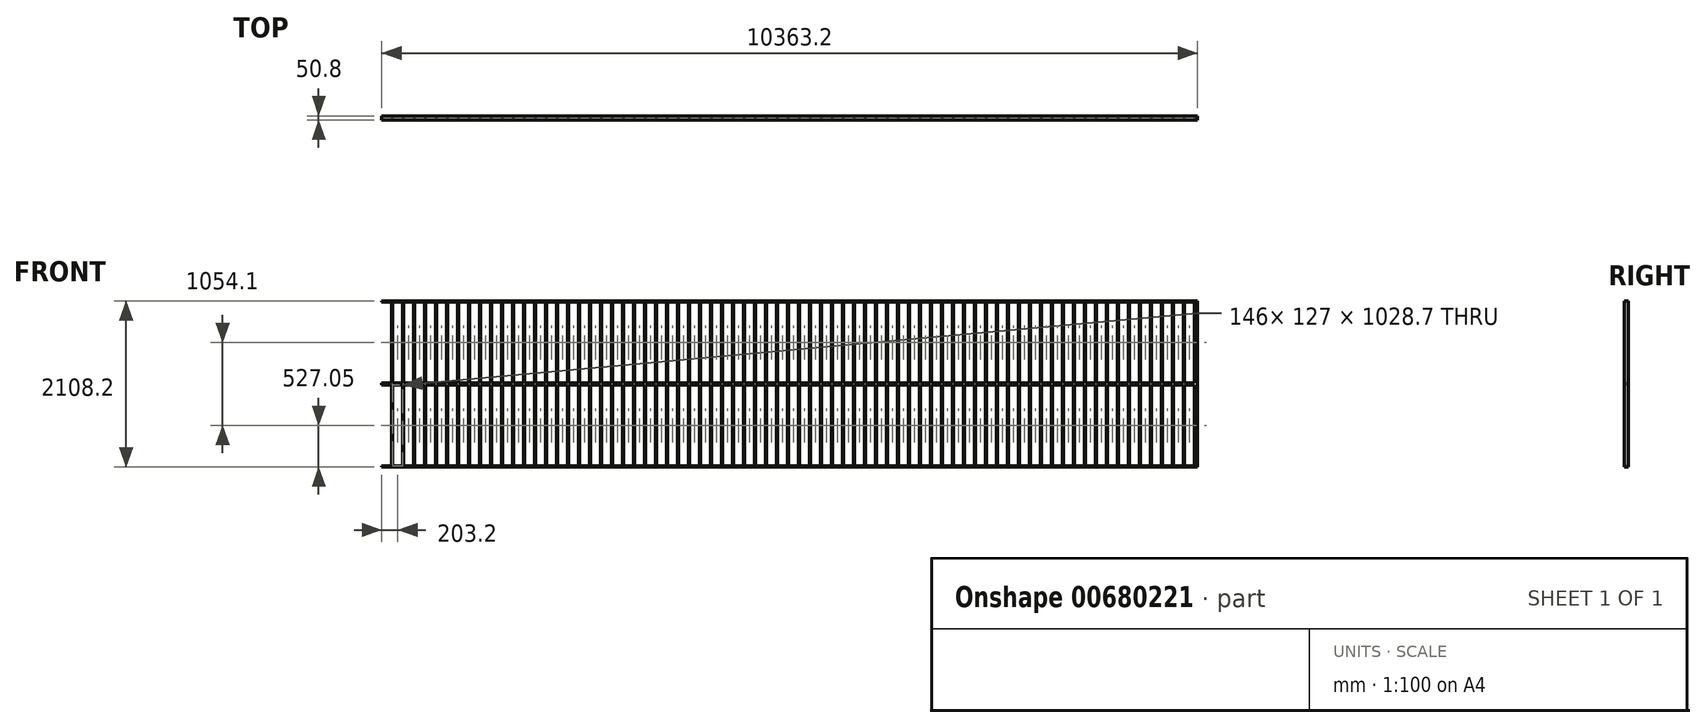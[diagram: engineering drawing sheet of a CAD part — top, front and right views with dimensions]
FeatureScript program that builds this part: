
annotation { "Feature Type Name" : "Feature", "Feature Type Description" : "" }
export const myFeature = defineFeature(function(context is Context, id is Id, definition is map)
    precondition{}
    {
        {
            var Q0;
            Q0=qCreatedBy(makeId("Front.planeOp"),FACE);
            var sketch = newSketch(context, id + "F0", { "sketchPlane" : qUnion([Q0])});
            skLineSegment(sketch, "E0", {"start": v(0, 0) * mm, "end": v(0, 2108.2) * mm});
            skLineSegment(sketch, "E1", {"start": v(0, 2108.2) * mm, "end": v(10363.2, 2108.2) * mm});
            skLineSegment(sketch, "E2", {"start": v(10363.2, 2108.2) * mm, "end": v(10363.2, 0) * mm});
            skLineSegment(sketch, "E3", {"start": v(10363.2, 0) * mm, "end": v(0, 0) * mm});
            skSolve(sketch);
        }
        {
            var Q0;
            Q0=makeQuery(id+"F0.imprint","IMPRINT",FACE,{"disambiguationData":[TD([[makeQuery(id+"F0.imprint","IMPRINT",EDGE,{"derivedFrom":sQuery(id+"F0.wireOp",EDGE,"E0")}),-1.0]])]});
            extrude(context, id + "F1", {"entities" : qUnion([Q0]), "depth" : 50.8 * mm, "offsetDistance" : 25.4 * mm});
        }
        {
            var Q0;
            Q0=makeQuery(id+"F1.opExtrude","CAP_FACE",FACE,{"disambiguationData":[OSD([sQuery(id+"F0.wireOp",EDGE,"E0"),sQuery(id+"F0.wireOp",EDGE,"E1"),sQuery(id+"F0.wireOp",EDGE,"E2"),sQuery(id+"F0.wireOp",EDGE,"E3")])],"isStart":false});
            var sketch = newSketch(context, id + "F2", { "sketchPlane" : qUnion([Q0])});
            skLineSegment(sketch, "E4", {"start": v(0, 12.7) * mm, "end": v(127, 12.7) * mm});
            skLineSegment(sketch, "E5", {"start": v(127, 12.7) * mm, "end": v(127, 1041.4) * mm});
            skLineSegment(sketch, "E6", {"start": v(127, 1041.4) * mm, "end": v(0, 1041.4) * mm});
            skLineSegment(sketch, "E7", {"start": v(0, 1041.4) * mm, "end": v(0, 0) * mm});
            skLineSegment(sketch, "E8", {"start": v(0, 2095.5) * mm, "end": v(127, 2095.5) * mm});
            skLineSegment(sketch, "E9", {"start": v(127, 2095.5) * mm, "end": v(127, 1066.8) * mm});
            skLineSegment(sketch, "E10", {"start": v(127, 1066.8) * mm, "end": v(0, 1066.8) * mm});
            skLineSegment(sketch, "E11", {"start": v(0, 1066.8) * mm, "end": v(0, 2095.5) * mm});
            skLineSegment(sketch, "E12.1.0.0", {"start": v(139.7, 1041.4) * mm, "end": v(139.7, 0) * mm});
            skLineSegment(sketch, "E12.1.0.1", {"start": v(139.7, 1066.8) * mm, "end": v(139.7, 2095.5) * mm});
            skLineSegment(sketch, "E12.1.0.2", {"start": v(266.7, 12.7) * mm, "end": v(266.7, 1041.4) * mm});
            skLineSegment(sketch, "E12.1.0.3", {"start": v(266.7, 2095.5) * mm, "end": v(266.7, 1066.8) * mm});
            skLineSegment(sketch, "E12.1.0.4", {"start": v(139.7, 2095.5) * mm, "end": v(266.7, 2095.5) * mm});
            skLineSegment(sketch, "E12.1.0.5", {"start": v(139.7, 12.7) * mm, "end": v(266.7, 12.7) * mm});
            skLineSegment(sketch, "E12.1.0.6", {"start": v(266.7, 1041.4) * mm, "end": v(139.7, 1041.4) * mm});
            skLineSegment(sketch, "E12.1.0.7", {"start": v(266.7, 1066.8) * mm, "end": v(139.7, 1066.8) * mm});
            skLineSegment(sketch, "E12.1.1.0", {"start": v(139.7, 1041.4) * mm, "end": v(139.7, 0) * mm});
            skLineSegment(sketch, "E12.1.1.1", {"start": v(139.7, 1066.8) * mm, "end": v(139.7, 2095.5) * mm});
            skLineSegment(sketch, "E12.1.1.2", {"start": v(266.7, 12.7) * mm, "end": v(266.7, 1041.4) * mm});
            skLineSegment(sketch, "E12.1.1.3", {"start": v(266.7, 2095.5) * mm, "end": v(266.7, 1066.8) * mm});
            skLineSegment(sketch, "E12.1.1.4", {"start": v(139.7, 2095.5) * mm, "end": v(266.7, 2095.5) * mm});
            skLineSegment(sketch, "E12.1.1.5", {"start": v(139.7, 12.7) * mm, "end": v(266.7, 12.7) * mm});
            skLineSegment(sketch, "E12.1.1.6", {"start": v(266.7, 1041.4) * mm, "end": v(139.7, 1041.4) * mm});
            skLineSegment(sketch, "E12.1.1.7", {"start": v(266.7, 1066.8) * mm, "end": v(139.7, 1066.8) * mm});
            skLineSegment(sketch, "E12.2.0.0", {"start": v(279.4, 1041.4) * mm, "end": v(279.4, 0) * mm});
            skLineSegment(sketch, "E12.2.0.1", {"start": v(279.4, 1066.8) * mm, "end": v(279.4, 2095.5) * mm});
            skLineSegment(sketch, "E12.2.0.2", {"start": v(406.4, 12.7) * mm, "end": v(406.4, 1041.4) * mm});
            skLineSegment(sketch, "E12.2.0.3", {"start": v(406.4, 2095.5) * mm, "end": v(406.4, 1066.8) * mm});
            skLineSegment(sketch, "E12.2.0.4", {"start": v(279.4, 2095.5) * mm, "end": v(406.4, 2095.5) * mm});
            skLineSegment(sketch, "E12.2.0.5", {"start": v(279.4, 12.7) * mm, "end": v(406.4, 12.7) * mm});
            skLineSegment(sketch, "E12.2.0.6", {"start": v(406.4, 1041.4) * mm, "end": v(279.4, 1041.4) * mm});
            skLineSegment(sketch, "E12.2.0.7", {"start": v(406.4, 1066.8) * mm, "end": v(279.4, 1066.8) * mm});
            skLineSegment(sketch, "E12.2.1.0", {"start": v(279.4, 1041.4) * mm, "end": v(279.4, 0) * mm});
            skLineSegment(sketch, "E12.2.1.1", {"start": v(279.4, 1066.8) * mm, "end": v(279.4, 2095.5) * mm});
            skLineSegment(sketch, "E12.2.1.2", {"start": v(406.4, 12.7) * mm, "end": v(406.4, 1041.4) * mm});
            skLineSegment(sketch, "E12.2.1.3", {"start": v(406.4, 2095.5) * mm, "end": v(406.4, 1066.8) * mm});
            skLineSegment(sketch, "E12.2.1.4", {"start": v(279.4, 2095.5) * mm, "end": v(406.4, 2095.5) * mm});
            skLineSegment(sketch, "E12.2.1.5", {"start": v(279.4, 12.7) * mm, "end": v(406.4, 12.7) * mm});
            skLineSegment(sketch, "E12.2.1.6", {"start": v(406.4, 1041.4) * mm, "end": v(279.4, 1041.4) * mm});
            skLineSegment(sketch, "E12.2.1.7", {"start": v(406.4, 1066.8) * mm, "end": v(279.4, 1066.8) * mm});
            skLineSegment(sketch, "E12.3.0.0", {"start": v(419.1, 1041.4) * mm, "end": v(419.1, 0) * mm});
            skLineSegment(sketch, "E12.3.0.1", {"start": v(419.1, 1066.8) * mm, "end": v(419.1, 2095.5) * mm});
            skLineSegment(sketch, "E12.3.0.2", {"start": v(546.1, 12.7) * mm, "end": v(546.1, 1041.4) * mm});
            skLineSegment(sketch, "E12.3.0.3", {"start": v(546.1, 2095.5) * mm, "end": v(546.1, 1066.8) * mm});
            skLineSegment(sketch, "E12.3.0.4", {"start": v(419.1, 2095.5) * mm, "end": v(546.1, 2095.5) * mm});
            skLineSegment(sketch, "E12.3.0.5", {"start": v(419.1, 12.7) * mm, "end": v(546.1, 12.7) * mm});
            skLineSegment(sketch, "E12.3.0.6", {"start": v(546.1, 1041.4) * mm, "end": v(419.1, 1041.4) * mm});
            skLineSegment(sketch, "E12.3.0.7", {"start": v(546.1, 1066.8) * mm, "end": v(419.1, 1066.8) * mm});
            skLineSegment(sketch, "E12.3.1.0", {"start": v(419.1, 1041.4) * mm, "end": v(419.1, 0) * mm});
            skLineSegment(sketch, "E12.3.1.1", {"start": v(419.1, 1066.8) * mm, "end": v(419.1, 2095.5) * mm});
            skLineSegment(sketch, "E12.3.1.2", {"start": v(546.1, 12.7) * mm, "end": v(546.1, 1041.4) * mm});
            skLineSegment(sketch, "E12.3.1.3", {"start": v(546.1, 2095.5) * mm, "end": v(546.1, 1066.8) * mm});
            skLineSegment(sketch, "E12.3.1.4", {"start": v(419.1, 2095.5) * mm, "end": v(546.1, 2095.5) * mm});
            skLineSegment(sketch, "E12.3.1.5", {"start": v(419.1, 12.7) * mm, "end": v(546.1, 12.7) * mm});
            skLineSegment(sketch, "E12.3.1.6", {"start": v(546.1, 1041.4) * mm, "end": v(419.1, 1041.4) * mm});
            skLineSegment(sketch, "E12.3.1.7", {"start": v(546.1, 1066.8) * mm, "end": v(419.1, 1066.8) * mm});
            skLineSegment(sketch, "E12.4.0.0", {"start": v(558.8, 1041.4) * mm, "end": v(558.8, 0) * mm});
            skLineSegment(sketch, "E12.4.0.1", {"start": v(558.8, 1066.8) * mm, "end": v(558.8, 2095.5) * mm});
            skLineSegment(sketch, "E12.4.0.2", {"start": v(685.8, 12.7) * mm, "end": v(685.8, 1041.4) * mm});
            skLineSegment(sketch, "E12.4.0.3", {"start": v(685.8, 2095.5) * mm, "end": v(685.8, 1066.8) * mm});
            skLineSegment(sketch, "E12.4.0.4", {"start": v(558.8, 2095.5) * mm, "end": v(685.8, 2095.5) * mm});
            skLineSegment(sketch, "E12.4.0.5", {"start": v(558.8, 12.7) * mm, "end": v(685.8, 12.7) * mm});
            skLineSegment(sketch, "E12.4.0.6", {"start": v(685.8, 1041.4) * mm, "end": v(558.8, 1041.4) * mm});
            skLineSegment(sketch, "E12.4.0.7", {"start": v(685.8, 1066.8) * mm, "end": v(558.8, 1066.8) * mm});
            skLineSegment(sketch, "E12.4.1.0", {"start": v(558.8, 1041.4) * mm, "end": v(558.8, 0) * mm});
            skLineSegment(sketch, "E12.4.1.1", {"start": v(558.8, 1066.8) * mm, "end": v(558.8, 2095.5) * mm});
            skLineSegment(sketch, "E12.4.1.2", {"start": v(685.8, 12.7) * mm, "end": v(685.8, 1041.4) * mm});
            skLineSegment(sketch, "E12.4.1.3", {"start": v(685.8, 2095.5) * mm, "end": v(685.8, 1066.8) * mm});
            skLineSegment(sketch, "E12.4.1.4", {"start": v(558.8, 2095.5) * mm, "end": v(685.8, 2095.5) * mm});
            skLineSegment(sketch, "E12.4.1.5", {"start": v(558.8, 12.7) * mm, "end": v(685.8, 12.7) * mm});
            skLineSegment(sketch, "E12.4.1.6", {"start": v(685.8, 1041.4) * mm, "end": v(558.8, 1041.4) * mm});
            skLineSegment(sketch, "E12.4.1.7", {"start": v(685.8, 1066.8) * mm, "end": v(558.8, 1066.8) * mm});
            skLineSegment(sketch, "E12.5.0.0", {"start": v(698.5, 1041.4) * mm, "end": v(698.5, 0) * mm});
            skLineSegment(sketch, "E12.5.0.1", {"start": v(698.5, 1066.8) * mm, "end": v(698.5, 2095.5) * mm});
            skLineSegment(sketch, "E12.5.0.2", {"start": v(825.5, 12.7) * mm, "end": v(825.5, 1041.4) * mm});
            skLineSegment(sketch, "E12.5.0.3", {"start": v(825.5, 2095.5) * mm, "end": v(825.5, 1066.8) * mm});
            skLineSegment(sketch, "E12.5.0.4", {"start": v(698.5, 2095.5) * mm, "end": v(825.5, 2095.5) * mm});
            skLineSegment(sketch, "E12.5.0.5", {"start": v(698.5, 12.7) * mm, "end": v(825.5, 12.7) * mm});
            skLineSegment(sketch, "E12.5.0.6", {"start": v(825.5, 1041.4) * mm, "end": v(698.5, 1041.4) * mm});
            skLineSegment(sketch, "E12.5.0.7", {"start": v(825.5, 1066.8) * mm, "end": v(698.5, 1066.8) * mm});
            skLineSegment(sketch, "E12.5.1.0", {"start": v(698.5, 1041.4) * mm, "end": v(698.5, 0) * mm});
            skLineSegment(sketch, "E12.5.1.1", {"start": v(698.5, 1066.8) * mm, "end": v(698.5, 2095.5) * mm});
            skLineSegment(sketch, "E12.5.1.2", {"start": v(825.5, 12.7) * mm, "end": v(825.5, 1041.4) * mm});
            skLineSegment(sketch, "E12.5.1.3", {"start": v(825.5, 2095.5) * mm, "end": v(825.5, 1066.8) * mm});
            skLineSegment(sketch, "E12.5.1.4", {"start": v(698.5, 2095.5) * mm, "end": v(825.5, 2095.5) * mm});
            skLineSegment(sketch, "E12.5.1.5", {"start": v(698.5, 12.7) * mm, "end": v(825.5, 12.7) * mm});
            skLineSegment(sketch, "E12.5.1.6", {"start": v(825.5, 1041.4) * mm, "end": v(698.5, 1041.4) * mm});
            skLineSegment(sketch, "E12.5.1.7", {"start": v(825.5, 1066.8) * mm, "end": v(698.5, 1066.8) * mm});
            skLineSegment(sketch, "E12.6.0.0", {"start": v(838.2, 1041.4) * mm, "end": v(838.2, 0) * mm});
            skLineSegment(sketch, "E12.6.0.1", {"start": v(838.2, 1066.8) * mm, "end": v(838.2, 2095.5) * mm});
            skLineSegment(sketch, "E12.6.0.2", {"start": v(965.2, 12.7) * mm, "end": v(965.2, 1041.4) * mm});
            skLineSegment(sketch, "E12.6.0.3", {"start": v(965.2, 2095.5) * mm, "end": v(965.2, 1066.8) * mm});
            skLineSegment(sketch, "E12.6.0.4", {"start": v(838.2, 2095.5) * mm, "end": v(965.2, 2095.5) * mm});
            skLineSegment(sketch, "E12.6.0.5", {"start": v(838.2, 12.7) * mm, "end": v(965.2, 12.7) * mm});
            skLineSegment(sketch, "E12.6.0.6", {"start": v(965.2, 1041.4) * mm, "end": v(838.2, 1041.4) * mm});
            skLineSegment(sketch, "E12.6.0.7", {"start": v(965.2, 1066.8) * mm, "end": v(838.2, 1066.8) * mm});
            skLineSegment(sketch, "E12.6.1.0", {"start": v(838.2, 1041.4) * mm, "end": v(838.2, 0) * mm});
            skLineSegment(sketch, "E12.6.1.1", {"start": v(838.2, 1066.8) * mm, "end": v(838.2, 2095.5) * mm});
            skLineSegment(sketch, "E12.6.1.2", {"start": v(965.2, 12.7) * mm, "end": v(965.2, 1041.4) * mm});
            skLineSegment(sketch, "E12.6.1.3", {"start": v(965.2, 2095.5) * mm, "end": v(965.2, 1066.8) * mm});
            skLineSegment(sketch, "E12.6.1.4", {"start": v(838.2, 2095.5) * mm, "end": v(965.2, 2095.5) * mm});
            skLineSegment(sketch, "E12.6.1.5", {"start": v(838.2, 12.7) * mm, "end": v(965.2, 12.7) * mm});
            skLineSegment(sketch, "E12.6.1.6", {"start": v(965.2, 1041.4) * mm, "end": v(838.2, 1041.4) * mm});
            skLineSegment(sketch, "E12.6.1.7", {"start": v(965.2, 1066.8) * mm, "end": v(838.2, 1066.8) * mm});
            skLineSegment(sketch, "E12.7.0.0", {"start": v(977.9, 1041.4) * mm, "end": v(977.9, 0) * mm});
            skLineSegment(sketch, "E12.7.0.1", {"start": v(977.9, 1066.8) * mm, "end": v(977.9, 2095.5) * mm});
            skLineSegment(sketch, "E12.7.0.2", {"start": v(1104.9, 12.7) * mm, "end": v(1104.9, 1041.4) * mm});
            skLineSegment(sketch, "E12.7.0.3", {"start": v(1104.9, 2095.5) * mm, "end": v(1104.9, 1066.8) * mm});
            skLineSegment(sketch, "E12.7.0.4", {"start": v(977.9, 2095.5) * mm, "end": v(1104.9, 2095.5) * mm});
            skLineSegment(sketch, "E12.7.0.5", {"start": v(977.9, 12.7) * mm, "end": v(1104.9, 12.7) * mm});
            skLineSegment(sketch, "E12.7.0.6", {"start": v(1104.9, 1041.4) * mm, "end": v(977.9, 1041.4) * mm});
            skLineSegment(sketch, "E12.7.0.7", {"start": v(1104.9, 1066.8) * mm, "end": v(977.9, 1066.8) * mm});
            skLineSegment(sketch, "E12.7.1.0", {"start": v(977.9, 1041.4) * mm, "end": v(977.9, 0) * mm});
            skLineSegment(sketch, "E12.7.1.1", {"start": v(977.9, 1066.8) * mm, "end": v(977.9, 2095.5) * mm});
            skLineSegment(sketch, "E12.7.1.2", {"start": v(1104.9, 12.7) * mm, "end": v(1104.9, 1041.4) * mm});
            skLineSegment(sketch, "E12.7.1.3", {"start": v(1104.9, 2095.5) * mm, "end": v(1104.9, 1066.8) * mm});
            skLineSegment(sketch, "E12.7.1.4", {"start": v(977.9, 2095.5) * mm, "end": v(1104.9, 2095.5) * mm});
            skLineSegment(sketch, "E12.7.1.5", {"start": v(977.9, 12.7) * mm, "end": v(1104.9, 12.7) * mm});
            skLineSegment(sketch, "E12.7.1.6", {"start": v(1104.9, 1041.4) * mm, "end": v(977.9, 1041.4) * mm});
            skLineSegment(sketch, "E12.7.1.7", {"start": v(1104.9, 1066.8) * mm, "end": v(977.9, 1066.8) * mm});
            skLineSegment(sketch, "E12.8.0.0", {"start": v(1117.6, 1041.4) * mm, "end": v(1117.6, 0) * mm});
            skLineSegment(sketch, "E12.8.0.1", {"start": v(1117.6, 1066.8) * mm, "end": v(1117.6, 2095.5) * mm});
            skLineSegment(sketch, "E12.8.0.2", {"start": v(1244.6, 12.7) * mm, "end": v(1244.6, 1041.4) * mm});
            skLineSegment(sketch, "E12.8.0.3", {"start": v(1244.6, 2095.5) * mm, "end": v(1244.6, 1066.8) * mm});
            skLineSegment(sketch, "E12.8.0.4", {"start": v(1117.6, 2095.5) * mm, "end": v(1244.6, 2095.5) * mm});
            skLineSegment(sketch, "E12.8.0.5", {"start": v(1117.6, 12.7) * mm, "end": v(1244.6, 12.7) * mm});
            skLineSegment(sketch, "E12.8.0.6", {"start": v(1244.6, 1041.4) * mm, "end": v(1117.6, 1041.4) * mm});
            skLineSegment(sketch, "E12.8.0.7", {"start": v(1244.6, 1066.8) * mm, "end": v(1117.6, 1066.8) * mm});
            skLineSegment(sketch, "E12.8.1.0", {"start": v(1117.6, 1041.4) * mm, "end": v(1117.6, 0) * mm});
            skLineSegment(sketch, "E12.8.1.1", {"start": v(1117.6, 1066.8) * mm, "end": v(1117.6, 2095.5) * mm});
            skLineSegment(sketch, "E12.8.1.2", {"start": v(1244.6, 12.7) * mm, "end": v(1244.6, 1041.4) * mm});
            skLineSegment(sketch, "E12.8.1.3", {"start": v(1244.6, 2095.5) * mm, "end": v(1244.6, 1066.8) * mm});
            skLineSegment(sketch, "E12.8.1.4", {"start": v(1117.6, 2095.5) * mm, "end": v(1244.6, 2095.5) * mm});
            skLineSegment(sketch, "E12.8.1.5", {"start": v(1117.6, 12.7) * mm, "end": v(1244.6, 12.7) * mm});
            skLineSegment(sketch, "E12.8.1.6", {"start": v(1244.6, 1041.4) * mm, "end": v(1117.6, 1041.4) * mm});
            skLineSegment(sketch, "E12.8.1.7", {"start": v(1244.6, 1066.8) * mm, "end": v(1117.6, 1066.8) * mm});
            skLineSegment(sketch, "E12.9.0.0", {"start": v(1257.3, 1041.4) * mm, "end": v(1257.3, 0) * mm});
            skLineSegment(sketch, "E12.9.0.1", {"start": v(1257.3, 1066.8) * mm, "end": v(1257.3, 2095.5) * mm});
            skLineSegment(sketch, "E12.9.0.2", {"start": v(1384.3, 12.7) * mm, "end": v(1384.3, 1041.4) * mm});
            skLineSegment(sketch, "E12.9.0.3", {"start": v(1384.3, 2095.5) * mm, "end": v(1384.3, 1066.8) * mm});
            skLineSegment(sketch, "E12.9.0.4", {"start": v(1257.3, 2095.5) * mm, "end": v(1384.3, 2095.5) * mm});
            skLineSegment(sketch, "E12.9.0.5", {"start": v(1257.3, 12.7) * mm, "end": v(1384.3, 12.7) * mm});
            skLineSegment(sketch, "E12.9.0.6", {"start": v(1384.3, 1041.4) * mm, "end": v(1257.3, 1041.4) * mm});
            skLineSegment(sketch, "E12.9.0.7", {"start": v(1384.3, 1066.8) * mm, "end": v(1257.3, 1066.8) * mm});
            skLineSegment(sketch, "E12.9.1.0", {"start": v(1257.3, 1041.4) * mm, "end": v(1257.3, 0) * mm});
            skLineSegment(sketch, "E12.9.1.1", {"start": v(1257.3, 1066.8) * mm, "end": v(1257.3, 2095.5) * mm});
            skLineSegment(sketch, "E12.9.1.2", {"start": v(1384.3, 12.7) * mm, "end": v(1384.3, 1041.4) * mm});
            skLineSegment(sketch, "E12.9.1.3", {"start": v(1384.3, 2095.5) * mm, "end": v(1384.3, 1066.8) * mm});
            skLineSegment(sketch, "E12.9.1.4", {"start": v(1257.3, 2095.5) * mm, "end": v(1384.3, 2095.5) * mm});
            skLineSegment(sketch, "E12.9.1.5", {"start": v(1257.3, 12.7) * mm, "end": v(1384.3, 12.7) * mm});
            skLineSegment(sketch, "E12.9.1.6", {"start": v(1384.3, 1041.4) * mm, "end": v(1257.3, 1041.4) * mm});
            skLineSegment(sketch, "E12.9.1.7", {"start": v(1384.3, 1066.8) * mm, "end": v(1257.3, 1066.8) * mm});
            skLineSegment(sketch, "E12.10.0.0", {"start": v(1397, 1041.4) * mm, "end": v(1397, 0) * mm});
            skLineSegment(sketch, "E12.10.0.1", {"start": v(1397, 1066.8) * mm, "end": v(1397, 2095.5) * mm});
            skLineSegment(sketch, "E12.10.0.2", {"start": v(1524, 12.7) * mm, "end": v(1524, 1041.4) * mm});
            skLineSegment(sketch, "E12.10.0.3", {"start": v(1524, 2095.5) * mm, "end": v(1524, 1066.8) * mm});
            skLineSegment(sketch, "E12.10.0.4", {"start": v(1397, 2095.5) * mm, "end": v(1524, 2095.5) * mm});
            skLineSegment(sketch, "E12.10.0.5", {"start": v(1397, 12.7) * mm, "end": v(1524, 12.7) * mm});
            skLineSegment(sketch, "E12.10.0.6", {"start": v(1524, 1041.4) * mm, "end": v(1397, 1041.4) * mm});
            skLineSegment(sketch, "E12.10.0.7", {"start": v(1524, 1066.8) * mm, "end": v(1397, 1066.8) * mm});
            skLineSegment(sketch, "E12.10.1.0", {"start": v(1397, 1041.4) * mm, "end": v(1397, 0) * mm});
            skLineSegment(sketch, "E12.10.1.1", {"start": v(1397, 1066.8) * mm, "end": v(1397, 2095.5) * mm});
            skLineSegment(sketch, "E12.10.1.2", {"start": v(1524, 12.7) * mm, "end": v(1524, 1041.4) * mm});
            skLineSegment(sketch, "E12.10.1.3", {"start": v(1524, 2095.5) * mm, "end": v(1524, 1066.8) * mm});
            skLineSegment(sketch, "E12.10.1.4", {"start": v(1397, 2095.5) * mm, "end": v(1524, 2095.5) * mm});
            skLineSegment(sketch, "E12.10.1.5", {"start": v(1397, 12.7) * mm, "end": v(1524, 12.7) * mm});
            skLineSegment(sketch, "E12.10.1.6", {"start": v(1524, 1041.4) * mm, "end": v(1397, 1041.4) * mm});
            skLineSegment(sketch, "E12.10.1.7", {"start": v(1524, 1066.8) * mm, "end": v(1397, 1066.8) * mm});
            skLineSegment(sketch, "E12.11.0.0", {"start": v(1536.7, 1041.4) * mm, "end": v(1536.7, 0) * mm});
            skLineSegment(sketch, "E12.11.0.1", {"start": v(1536.7, 1066.8) * mm, "end": v(1536.7, 2095.5) * mm});
            skLineSegment(sketch, "E12.11.0.2", {"start": v(1663.7, 12.7) * mm, "end": v(1663.7, 1041.4) * mm});
            skLineSegment(sketch, "E12.11.0.3", {"start": v(1663.7, 2095.5) * mm, "end": v(1663.7, 1066.8) * mm});
            skLineSegment(sketch, "E12.11.0.4", {"start": v(1536.7, 2095.5) * mm, "end": v(1663.7, 2095.5) * mm});
            skLineSegment(sketch, "E12.11.0.5", {"start": v(1536.7, 12.7) * mm, "end": v(1663.7, 12.7) * mm});
            skLineSegment(sketch, "E12.11.0.6", {"start": v(1663.7, 1041.4) * mm, "end": v(1536.7, 1041.4) * mm});
            skLineSegment(sketch, "E12.11.0.7", {"start": v(1663.7, 1066.8) * mm, "end": v(1536.7, 1066.8) * mm});
            skLineSegment(sketch, "E12.11.1.0", {"start": v(1536.7, 1041.4) * mm, "end": v(1536.7, 0) * mm});
            skLineSegment(sketch, "E12.11.1.1", {"start": v(1536.7, 1066.8) * mm, "end": v(1536.7, 2095.5) * mm});
            skLineSegment(sketch, "E12.11.1.2", {"start": v(1663.7, 12.7) * mm, "end": v(1663.7, 1041.4) * mm});
            skLineSegment(sketch, "E12.11.1.3", {"start": v(1663.7, 2095.5) * mm, "end": v(1663.7, 1066.8) * mm});
            skLineSegment(sketch, "E12.11.1.4", {"start": v(1536.7, 2095.5) * mm, "end": v(1663.7, 2095.5) * mm});
            skLineSegment(sketch, "E12.11.1.5", {"start": v(1536.7, 12.7) * mm, "end": v(1663.7, 12.7) * mm});
            skLineSegment(sketch, "E12.11.1.6", {"start": v(1663.7, 1041.4) * mm, "end": v(1536.7, 1041.4) * mm});
            skLineSegment(sketch, "E12.11.1.7", {"start": v(1663.7, 1066.8) * mm, "end": v(1536.7, 1066.8) * mm});
            skLineSegment(sketch, "E12.12.0.0", {"start": v(1676.4, 1041.4) * mm, "end": v(1676.4, 0) * mm});
            skLineSegment(sketch, "E12.12.0.1", {"start": v(1676.4, 1066.8) * mm, "end": v(1676.4, 2095.5) * mm});
            skLineSegment(sketch, "E12.12.0.2", {"start": v(1803.4, 12.7) * mm, "end": v(1803.4, 1041.4) * mm});
            skLineSegment(sketch, "E12.12.0.3", {"start": v(1803.4, 2095.5) * mm, "end": v(1803.4, 1066.8) * mm});
            skLineSegment(sketch, "E12.12.0.4", {"start": v(1676.4, 2095.5) * mm, "end": v(1803.4, 2095.5) * mm});
            skLineSegment(sketch, "E12.12.0.5", {"start": v(1676.4, 12.7) * mm, "end": v(1803.4, 12.7) * mm});
            skLineSegment(sketch, "E12.12.0.6", {"start": v(1803.4, 1041.4) * mm, "end": v(1676.4, 1041.4) * mm});
            skLineSegment(sketch, "E12.12.0.7", {"start": v(1803.4, 1066.8) * mm, "end": v(1676.4, 1066.8) * mm});
            skLineSegment(sketch, "E12.12.1.0", {"start": v(1676.4, 1041.4) * mm, "end": v(1676.4, 0) * mm});
            skLineSegment(sketch, "E12.12.1.1", {"start": v(1676.4, 1066.8) * mm, "end": v(1676.4, 2095.5) * mm});
            skLineSegment(sketch, "E12.12.1.2", {"start": v(1803.4, 12.7) * mm, "end": v(1803.4, 1041.4) * mm});
            skLineSegment(sketch, "E12.12.1.3", {"start": v(1803.4, 2095.5) * mm, "end": v(1803.4, 1066.8) * mm});
            skLineSegment(sketch, "E12.12.1.4", {"start": v(1676.4, 2095.5) * mm, "end": v(1803.4, 2095.5) * mm});
            skLineSegment(sketch, "E12.12.1.5", {"start": v(1676.4, 12.7) * mm, "end": v(1803.4, 12.7) * mm});
            skLineSegment(sketch, "E12.12.1.6", {"start": v(1803.4, 1041.4) * mm, "end": v(1676.4, 1041.4) * mm});
            skLineSegment(sketch, "E12.12.1.7", {"start": v(1803.4, 1066.8) * mm, "end": v(1676.4, 1066.8) * mm});
            skLineSegment(sketch, "E12.13.0.0", {"start": v(1816.1, 1041.4) * mm, "end": v(1816.1, 0) * mm});
            skLineSegment(sketch, "E12.13.0.1", {"start": v(1816.1, 1066.8) * mm, "end": v(1816.1, 2095.5) * mm});
            skLineSegment(sketch, "E12.13.0.2", {"start": v(1943.1, 12.7) * mm, "end": v(1943.1, 1041.4) * mm});
            skLineSegment(sketch, "E12.13.0.3", {"start": v(1943.1, 2095.5) * mm, "end": v(1943.1, 1066.8) * mm});
            skLineSegment(sketch, "E12.13.0.4", {"start": v(1816.1, 2095.5) * mm, "end": v(1943.1, 2095.5) * mm});
            skLineSegment(sketch, "E12.13.0.5", {"start": v(1816.1, 12.7) * mm, "end": v(1943.1, 12.7) * mm});
            skLineSegment(sketch, "E12.13.0.6", {"start": v(1943.1, 1041.4) * mm, "end": v(1816.1, 1041.4) * mm});
            skLineSegment(sketch, "E12.13.0.7", {"start": v(1943.1, 1066.8) * mm, "end": v(1816.1, 1066.8) * mm});
            skLineSegment(sketch, "E12.13.1.0", {"start": v(1816.1, 1041.4) * mm, "end": v(1816.1, 0) * mm});
            skLineSegment(sketch, "E12.13.1.1", {"start": v(1816.1, 1066.8) * mm, "end": v(1816.1, 2095.5) * mm});
            skLineSegment(sketch, "E12.13.1.2", {"start": v(1943.1, 12.7) * mm, "end": v(1943.1, 1041.4) * mm});
            skLineSegment(sketch, "E12.13.1.3", {"start": v(1943.1, 2095.5) * mm, "end": v(1943.1, 1066.8) * mm});
            skLineSegment(sketch, "E12.13.1.4", {"start": v(1816.1, 2095.5) * mm, "end": v(1943.1, 2095.5) * mm});
            skLineSegment(sketch, "E12.13.1.5", {"start": v(1816.1, 12.7) * mm, "end": v(1943.1, 12.7) * mm});
            skLineSegment(sketch, "E12.13.1.6", {"start": v(1943.1, 1041.4) * mm, "end": v(1816.1, 1041.4) * mm});
            skLineSegment(sketch, "E12.13.1.7", {"start": v(1943.1, 1066.8) * mm, "end": v(1816.1, 1066.8) * mm});
            skLineSegment(sketch, "E12.14.0.0", {"start": v(1955.8, 1041.4) * mm, "end": v(1955.8, 0) * mm});
            skLineSegment(sketch, "E12.14.0.1", {"start": v(1955.8, 1066.8) * mm, "end": v(1955.8, 2095.5) * mm});
            skLineSegment(sketch, "E12.14.0.2", {"start": v(2082.8, 12.7) * mm, "end": v(2082.8, 1041.4) * mm});
            skLineSegment(sketch, "E12.14.0.3", {"start": v(2082.8, 2095.5) * mm, "end": v(2082.8, 1066.8) * mm});
            skLineSegment(sketch, "E12.14.0.4", {"start": v(1955.8, 2095.5) * mm, "end": v(2082.8, 2095.5) * mm});
            skLineSegment(sketch, "E12.14.0.5", {"start": v(1955.8, 12.7) * mm, "end": v(2082.8, 12.7) * mm});
            skLineSegment(sketch, "E12.14.0.6", {"start": v(2082.8, 1041.4) * mm, "end": v(1955.8, 1041.4) * mm});
            skLineSegment(sketch, "E12.14.0.7", {"start": v(2082.8, 1066.8) * mm, "end": v(1955.8, 1066.8) * mm});
            skLineSegment(sketch, "E12.14.1.0", {"start": v(1955.8, 1041.4) * mm, "end": v(1955.8, 0) * mm});
            skLineSegment(sketch, "E12.14.1.1", {"start": v(1955.8, 1066.8) * mm, "end": v(1955.8, 2095.5) * mm});
            skLineSegment(sketch, "E12.14.1.2", {"start": v(2082.8, 12.7) * mm, "end": v(2082.8, 1041.4) * mm});
            skLineSegment(sketch, "E12.14.1.3", {"start": v(2082.8, 2095.5) * mm, "end": v(2082.8, 1066.8) * mm});
            skLineSegment(sketch, "E12.14.1.4", {"start": v(1955.8, 2095.5) * mm, "end": v(2082.8, 2095.5) * mm});
            skLineSegment(sketch, "E12.14.1.5", {"start": v(1955.8, 12.7) * mm, "end": v(2082.8, 12.7) * mm});
            skLineSegment(sketch, "E12.14.1.6", {"start": v(2082.8, 1041.4) * mm, "end": v(1955.8, 1041.4) * mm});
            skLineSegment(sketch, "E12.14.1.7", {"start": v(2082.8, 1066.8) * mm, "end": v(1955.8, 1066.8) * mm});
            skLineSegment(sketch, "E12.15.0.0", {"start": v(2095.5, 1041.4) * mm, "end": v(2095.5, 0) * mm});
            skLineSegment(sketch, "E12.15.0.1", {"start": v(2095.5, 1066.8) * mm, "end": v(2095.5, 2095.5) * mm});
            skLineSegment(sketch, "E12.15.0.2", {"start": v(2222.5, 12.7) * mm, "end": v(2222.5, 1041.4) * mm});
            skLineSegment(sketch, "E12.15.0.3", {"start": v(2222.5, 2095.5) * mm, "end": v(2222.5, 1066.8) * mm});
            skLineSegment(sketch, "E12.15.0.4", {"start": v(2095.5, 2095.5) * mm, "end": v(2222.5, 2095.5) * mm});
            skLineSegment(sketch, "E12.15.0.5", {"start": v(2095.5, 12.7) * mm, "end": v(2222.5, 12.7) * mm});
            skLineSegment(sketch, "E12.15.0.6", {"start": v(2222.5, 1041.4) * mm, "end": v(2095.5, 1041.4) * mm});
            skLineSegment(sketch, "E12.15.0.7", {"start": v(2222.5, 1066.8) * mm, "end": v(2095.5, 1066.8) * mm});
            skLineSegment(sketch, "E12.15.1.0", {"start": v(2095.5, 1041.4) * mm, "end": v(2095.5, 0) * mm});
            skLineSegment(sketch, "E12.15.1.1", {"start": v(2095.5, 1066.8) * mm, "end": v(2095.5, 2095.5) * mm});
            skLineSegment(sketch, "E12.15.1.2", {"start": v(2222.5, 12.7) * mm, "end": v(2222.5, 1041.4) * mm});
            skLineSegment(sketch, "E12.15.1.3", {"start": v(2222.5, 2095.5) * mm, "end": v(2222.5, 1066.8) * mm});
            skLineSegment(sketch, "E12.15.1.4", {"start": v(2095.5, 2095.5) * mm, "end": v(2222.5, 2095.5) * mm});
            skLineSegment(sketch, "E12.15.1.5", {"start": v(2095.5, 12.7) * mm, "end": v(2222.5, 12.7) * mm});
            skLineSegment(sketch, "E12.15.1.6", {"start": v(2222.5, 1041.4) * mm, "end": v(2095.5, 1041.4) * mm});
            skLineSegment(sketch, "E12.15.1.7", {"start": v(2222.5, 1066.8) * mm, "end": v(2095.5, 1066.8) * mm});
            skLineSegment(sketch, "E12.16.0.0", {"start": v(2235.2, 1041.4) * mm, "end": v(2235.2, 0) * mm});
            skLineSegment(sketch, "E12.16.0.1", {"start": v(2235.2, 1066.8) * mm, "end": v(2235.2, 2095.5) * mm});
            skLineSegment(sketch, "E12.16.0.2", {"start": v(2362.2, 12.7) * mm, "end": v(2362.2, 1041.4) * mm});
            skLineSegment(sketch, "E12.16.0.3", {"start": v(2362.2, 2095.5) * mm, "end": v(2362.2, 1066.8) * mm});
            skLineSegment(sketch, "E12.16.0.4", {"start": v(2235.2, 2095.5) * mm, "end": v(2362.2, 2095.5) * mm});
            skLineSegment(sketch, "E12.16.0.5", {"start": v(2235.2, 12.7) * mm, "end": v(2362.2, 12.7) * mm});
            skLineSegment(sketch, "E12.16.0.6", {"start": v(2362.2, 1041.4) * mm, "end": v(2235.2, 1041.4) * mm});
            skLineSegment(sketch, "E12.16.0.7", {"start": v(2362.2, 1066.8) * mm, "end": v(2235.2, 1066.8) * mm});
            skLineSegment(sketch, "E12.16.1.0", {"start": v(2235.2, 1041.4) * mm, "end": v(2235.2, 0) * mm});
            skLineSegment(sketch, "E12.16.1.1", {"start": v(2235.2, 1066.8) * mm, "end": v(2235.2, 2095.5) * mm});
            skLineSegment(sketch, "E12.16.1.2", {"start": v(2362.2, 12.7) * mm, "end": v(2362.2, 1041.4) * mm});
            skLineSegment(sketch, "E12.16.1.3", {"start": v(2362.2, 2095.5) * mm, "end": v(2362.2, 1066.8) * mm});
            skLineSegment(sketch, "E12.16.1.4", {"start": v(2235.2, 2095.5) * mm, "end": v(2362.2, 2095.5) * mm});
            skLineSegment(sketch, "E12.16.1.5", {"start": v(2235.2, 12.7) * mm, "end": v(2362.2, 12.7) * mm});
            skLineSegment(sketch, "E12.16.1.6", {"start": v(2362.2, 1041.4) * mm, "end": v(2235.2, 1041.4) * mm});
            skLineSegment(sketch, "E12.16.1.7", {"start": v(2362.2, 1066.8) * mm, "end": v(2235.2, 1066.8) * mm});
            skLineSegment(sketch, "E12.17.0.0", {"start": v(2374.9, 1041.4) * mm, "end": v(2374.9, 0) * mm});
            skLineSegment(sketch, "E12.17.0.1", {"start": v(2374.9, 1066.8) * mm, "end": v(2374.9, 2095.5) * mm});
            skLineSegment(sketch, "E12.17.0.2", {"start": v(2501.9, 12.7) * mm, "end": v(2501.9, 1041.4) * mm});
            skLineSegment(sketch, "E12.17.0.3", {"start": v(2501.9, 2095.5) * mm, "end": v(2501.9, 1066.8) * mm});
            skLineSegment(sketch, "E12.17.0.4", {"start": v(2374.9, 2095.5) * mm, "end": v(2501.9, 2095.5) * mm});
            skLineSegment(sketch, "E12.17.0.5", {"start": v(2374.9, 12.7) * mm, "end": v(2501.9, 12.7) * mm});
            skLineSegment(sketch, "E12.17.0.6", {"start": v(2501.9, 1041.4) * mm, "end": v(2374.9, 1041.4) * mm});
            skLineSegment(sketch, "E12.17.0.7", {"start": v(2501.9, 1066.8) * mm, "end": v(2374.9, 1066.8) * mm});
            skLineSegment(sketch, "E12.17.1.0", {"start": v(2374.9, 1041.4) * mm, "end": v(2374.9, 0) * mm});
            skLineSegment(sketch, "E12.17.1.1", {"start": v(2374.9, 1066.8) * mm, "end": v(2374.9, 2095.5) * mm});
            skLineSegment(sketch, "E12.17.1.2", {"start": v(2501.9, 12.7) * mm, "end": v(2501.9, 1041.4) * mm});
            skLineSegment(sketch, "E12.17.1.3", {"start": v(2501.9, 2095.5) * mm, "end": v(2501.9, 1066.8) * mm});
            skLineSegment(sketch, "E12.17.1.4", {"start": v(2374.9, 2095.5) * mm, "end": v(2501.9, 2095.5) * mm});
            skLineSegment(sketch, "E12.17.1.5", {"start": v(2374.9, 12.7) * mm, "end": v(2501.9, 12.7) * mm});
            skLineSegment(sketch, "E12.17.1.6", {"start": v(2501.9, 1041.4) * mm, "end": v(2374.9, 1041.4) * mm});
            skLineSegment(sketch, "E12.17.1.7", {"start": v(2501.9, 1066.8) * mm, "end": v(2374.9, 1066.8) * mm});
            skLineSegment(sketch, "E12.18.0.0", {"start": v(2514.6, 1041.4) * mm, "end": v(2514.6, 0) * mm});
            skLineSegment(sketch, "E12.18.0.1", {"start": v(2514.6, 1066.8) * mm, "end": v(2514.6, 2095.5) * mm});
            skLineSegment(sketch, "E12.18.0.2", {"start": v(2641.6, 12.7) * mm, "end": v(2641.6, 1041.4) * mm});
            skLineSegment(sketch, "E12.18.0.3", {"start": v(2641.6, 2095.5) * mm, "end": v(2641.6, 1066.8) * mm});
            skLineSegment(sketch, "E12.18.0.4", {"start": v(2514.6, 2095.5) * mm, "end": v(2641.6, 2095.5) * mm});
            skLineSegment(sketch, "E12.18.0.5", {"start": v(2514.6, 12.7) * mm, "end": v(2641.6, 12.7) * mm});
            skLineSegment(sketch, "E12.18.0.6", {"start": v(2641.6, 1041.4) * mm, "end": v(2514.6, 1041.4) * mm});
            skLineSegment(sketch, "E12.18.0.7", {"start": v(2641.6, 1066.8) * mm, "end": v(2514.6, 1066.8) * mm});
            skLineSegment(sketch, "E12.18.1.0", {"start": v(2514.6, 1041.4) * mm, "end": v(2514.6, 0) * mm});
            skLineSegment(sketch, "E12.18.1.1", {"start": v(2514.6, 1066.8) * mm, "end": v(2514.6, 2095.5) * mm});
            skLineSegment(sketch, "E12.18.1.2", {"start": v(2641.6, 12.7) * mm, "end": v(2641.6, 1041.4) * mm});
            skLineSegment(sketch, "E12.18.1.3", {"start": v(2641.6, 2095.5) * mm, "end": v(2641.6, 1066.8) * mm});
            skLineSegment(sketch, "E12.18.1.4", {"start": v(2514.6, 2095.5) * mm, "end": v(2641.6, 2095.5) * mm});
            skLineSegment(sketch, "E12.18.1.5", {"start": v(2514.6, 12.7) * mm, "end": v(2641.6, 12.7) * mm});
            skLineSegment(sketch, "E12.18.1.6", {"start": v(2641.6, 1041.4) * mm, "end": v(2514.6, 1041.4) * mm});
            skLineSegment(sketch, "E12.18.1.7", {"start": v(2641.6, 1066.8) * mm, "end": v(2514.6, 1066.8) * mm});
            skLineSegment(sketch, "E12.19.0.0", {"start": v(2654.3, 1041.4) * mm, "end": v(2654.3, 0) * mm});
            skLineSegment(sketch, "E12.19.0.1", {"start": v(2654.3, 1066.8) * mm, "end": v(2654.3, 2095.5) * mm});
            skLineSegment(sketch, "E12.19.0.2", {"start": v(2781.3, 12.7) * mm, "end": v(2781.3, 1041.4) * mm});
            skLineSegment(sketch, "E12.19.0.3", {"start": v(2781.3, 2095.5) * mm, "end": v(2781.3, 1066.8) * mm});
            skLineSegment(sketch, "E12.19.0.4", {"start": v(2654.3, 2095.5) * mm, "end": v(2781.3, 2095.5) * mm});
            skLineSegment(sketch, "E12.19.0.5", {"start": v(2654.3, 12.7) * mm, "end": v(2781.3, 12.7) * mm});
            skLineSegment(sketch, "E12.19.0.6", {"start": v(2781.3, 1041.4) * mm, "end": v(2654.3, 1041.4) * mm});
            skLineSegment(sketch, "E12.19.0.7", {"start": v(2781.3, 1066.8) * mm, "end": v(2654.3, 1066.8) * mm});
            skLineSegment(sketch, "E12.19.1.0", {"start": v(2654.3, 1041.4) * mm, "end": v(2654.3, 0) * mm});
            skLineSegment(sketch, "E12.19.1.1", {"start": v(2654.3, 1066.8) * mm, "end": v(2654.3, 2095.5) * mm});
            skLineSegment(sketch, "E12.19.1.2", {"start": v(2781.3, 12.7) * mm, "end": v(2781.3, 1041.4) * mm});
            skLineSegment(sketch, "E12.19.1.3", {"start": v(2781.3, 2095.5) * mm, "end": v(2781.3, 1066.8) * mm});
            skLineSegment(sketch, "E12.19.1.4", {"start": v(2654.3, 2095.5) * mm, "end": v(2781.3, 2095.5) * mm});
            skLineSegment(sketch, "E12.19.1.5", {"start": v(2654.3, 12.7) * mm, "end": v(2781.3, 12.7) * mm});
            skLineSegment(sketch, "E12.19.1.6", {"start": v(2781.3, 1041.4) * mm, "end": v(2654.3, 1041.4) * mm});
            skLineSegment(sketch, "E12.19.1.7", {"start": v(2781.3, 1066.8) * mm, "end": v(2654.3, 1066.8) * mm});
            skLineSegment(sketch, "E12.20.0.0", {"start": v(2794, 1041.4) * mm, "end": v(2794, 0) * mm});
            skLineSegment(sketch, "E12.20.0.1", {"start": v(2794, 1066.8) * mm, "end": v(2794, 2095.5) * mm});
            skLineSegment(sketch, "E12.20.0.2", {"start": v(2921, 12.7) * mm, "end": v(2921, 1041.4) * mm});
            skLineSegment(sketch, "E12.20.0.3", {"start": v(2921, 2095.5) * mm, "end": v(2921, 1066.8) * mm});
            skLineSegment(sketch, "E12.20.0.4", {"start": v(2794, 2095.5) * mm, "end": v(2921, 2095.5) * mm});
            skLineSegment(sketch, "E12.20.0.5", {"start": v(2794, 12.7) * mm, "end": v(2921, 12.7) * mm});
            skLineSegment(sketch, "E12.20.0.6", {"start": v(2921, 1041.4) * mm, "end": v(2794, 1041.4) * mm});
            skLineSegment(sketch, "E12.20.0.7", {"start": v(2921, 1066.8) * mm, "end": v(2794, 1066.8) * mm});
            skLineSegment(sketch, "E12.20.1.0", {"start": v(2794, 1041.4) * mm, "end": v(2794, 0) * mm});
            skLineSegment(sketch, "E12.20.1.1", {"start": v(2794, 1066.8) * mm, "end": v(2794, 2095.5) * mm});
            skLineSegment(sketch, "E12.20.1.2", {"start": v(2921, 12.7) * mm, "end": v(2921, 1041.4) * mm});
            skLineSegment(sketch, "E12.20.1.3", {"start": v(2921, 2095.5) * mm, "end": v(2921, 1066.8) * mm});
            skLineSegment(sketch, "E12.20.1.4", {"start": v(2794, 2095.5) * mm, "end": v(2921, 2095.5) * mm});
            skLineSegment(sketch, "E12.20.1.5", {"start": v(2794, 12.7) * mm, "end": v(2921, 12.7) * mm});
            skLineSegment(sketch, "E12.20.1.6", {"start": v(2921, 1041.4) * mm, "end": v(2794, 1041.4) * mm});
            skLineSegment(sketch, "E12.20.1.7", {"start": v(2921, 1066.8) * mm, "end": v(2794, 1066.8) * mm});
            skLineSegment(sketch, "E12.21.0.0", {"start": v(2933.7, 1041.4) * mm, "end": v(2933.7, 0) * mm});
            skLineSegment(sketch, "E12.21.0.1", {"start": v(2933.7, 1066.8) * mm, "end": v(2933.7, 2095.5) * mm});
            skLineSegment(sketch, "E12.21.0.2", {"start": v(3060.7, 12.7) * mm, "end": v(3060.7, 1041.4) * mm});
            skLineSegment(sketch, "E12.21.0.3", {"start": v(3060.7, 2095.5) * mm, "end": v(3060.7, 1066.8) * mm});
            skLineSegment(sketch, "E12.21.0.4", {"start": v(2933.7, 2095.5) * mm, "end": v(3060.7, 2095.5) * mm});
            skLineSegment(sketch, "E12.21.0.5", {"start": v(2933.7, 12.7) * mm, "end": v(3060.7, 12.7) * mm});
            skLineSegment(sketch, "E12.21.0.6", {"start": v(3060.7, 1041.4) * mm, "end": v(2933.7, 1041.4) * mm});
            skLineSegment(sketch, "E12.21.0.7", {"start": v(3060.7, 1066.8) * mm, "end": v(2933.7, 1066.8) * mm});
            skLineSegment(sketch, "E12.21.1.0", {"start": v(2933.7, 1041.4) * mm, "end": v(2933.7, 0) * mm});
            skLineSegment(sketch, "E12.21.1.1", {"start": v(2933.7, 1066.8) * mm, "end": v(2933.7, 2095.5) * mm});
            skLineSegment(sketch, "E12.21.1.2", {"start": v(3060.7, 12.7) * mm, "end": v(3060.7, 1041.4) * mm});
            skLineSegment(sketch, "E12.21.1.3", {"start": v(3060.7, 2095.5) * mm, "end": v(3060.7, 1066.8) * mm});
            skLineSegment(sketch, "E12.21.1.4", {"start": v(2933.7, 2095.5) * mm, "end": v(3060.7, 2095.5) * mm});
            skLineSegment(sketch, "E12.21.1.5", {"start": v(2933.7, 12.7) * mm, "end": v(3060.7, 12.7) * mm});
            skLineSegment(sketch, "E12.21.1.6", {"start": v(3060.7, 1041.4) * mm, "end": v(2933.7, 1041.4) * mm});
            skLineSegment(sketch, "E12.21.1.7", {"start": v(3060.7, 1066.8) * mm, "end": v(2933.7, 1066.8) * mm});
            skLineSegment(sketch, "E12.22.0.0", {"start": v(3073.4, 1041.4) * mm, "end": v(3073.4, 0) * mm});
            skLineSegment(sketch, "E12.22.0.1", {"start": v(3073.4, 1066.8) * mm, "end": v(3073.4, 2095.5) * mm});
            skLineSegment(sketch, "E12.22.0.2", {"start": v(3200.4, 12.7) * mm, "end": v(3200.4, 1041.4) * mm});
            skLineSegment(sketch, "E12.22.0.3", {"start": v(3200.4, 2095.5) * mm, "end": v(3200.4, 1066.8) * mm});
            skLineSegment(sketch, "E12.22.0.4", {"start": v(3073.4, 2095.5) * mm, "end": v(3200.4, 2095.5) * mm});
            skLineSegment(sketch, "E12.22.0.5", {"start": v(3073.4, 12.7) * mm, "end": v(3200.4, 12.7) * mm});
            skLineSegment(sketch, "E12.22.0.6", {"start": v(3200.4, 1041.4) * mm, "end": v(3073.4, 1041.4) * mm});
            skLineSegment(sketch, "E12.22.0.7", {"start": v(3200.4, 1066.8) * mm, "end": v(3073.4, 1066.8) * mm});
            skLineSegment(sketch, "E12.22.1.0", {"start": v(3073.4, 1041.4) * mm, "end": v(3073.4, 0) * mm});
            skLineSegment(sketch, "E12.22.1.1", {"start": v(3073.4, 1066.8) * mm, "end": v(3073.4, 2095.5) * mm});
            skLineSegment(sketch, "E12.22.1.2", {"start": v(3200.4, 12.7) * mm, "end": v(3200.4, 1041.4) * mm});
            skLineSegment(sketch, "E12.22.1.3", {"start": v(3200.4, 2095.5) * mm, "end": v(3200.4, 1066.8) * mm});
            skLineSegment(sketch, "E12.22.1.4", {"start": v(3073.4, 2095.5) * mm, "end": v(3200.4, 2095.5) * mm});
            skLineSegment(sketch, "E12.22.1.5", {"start": v(3073.4, 12.7) * mm, "end": v(3200.4, 12.7) * mm});
            skLineSegment(sketch, "E12.22.1.6", {"start": v(3200.4, 1041.4) * mm, "end": v(3073.4, 1041.4) * mm});
            skLineSegment(sketch, "E12.22.1.7", {"start": v(3200.4, 1066.8) * mm, "end": v(3073.4, 1066.8) * mm});
            skLineSegment(sketch, "E12.23.0.0", {"start": v(3213.1, 1041.4) * mm, "end": v(3213.1, 0) * mm});
            skLineSegment(sketch, "E12.23.0.1", {"start": v(3213.1, 1066.8) * mm, "end": v(3213.1, 2095.5) * mm});
            skLineSegment(sketch, "E12.23.0.2", {"start": v(3340.1, 12.7) * mm, "end": v(3340.1, 1041.4) * mm});
            skLineSegment(sketch, "E12.23.0.3", {"start": v(3340.1, 2095.5) * mm, "end": v(3340.1, 1066.8) * mm});
            skLineSegment(sketch, "E12.23.0.4", {"start": v(3213.1, 2095.5) * mm, "end": v(3340.1, 2095.5) * mm});
            skLineSegment(sketch, "E12.23.0.5", {"start": v(3213.1, 12.7) * mm, "end": v(3340.1, 12.7) * mm});
            skLineSegment(sketch, "E12.23.0.6", {"start": v(3340.1, 1041.4) * mm, "end": v(3213.1, 1041.4) * mm});
            skLineSegment(sketch, "E12.23.0.7", {"start": v(3340.1, 1066.8) * mm, "end": v(3213.1, 1066.8) * mm});
            skLineSegment(sketch, "E12.23.1.0", {"start": v(3213.1, 1041.4) * mm, "end": v(3213.1, 0) * mm});
            skLineSegment(sketch, "E12.23.1.1", {"start": v(3213.1, 1066.8) * mm, "end": v(3213.1, 2095.5) * mm});
            skLineSegment(sketch, "E12.23.1.2", {"start": v(3340.1, 12.7) * mm, "end": v(3340.1, 1041.4) * mm});
            skLineSegment(sketch, "E12.23.1.3", {"start": v(3340.1, 2095.5) * mm, "end": v(3340.1, 1066.8) * mm});
            skLineSegment(sketch, "E12.23.1.4", {"start": v(3213.1, 2095.5) * mm, "end": v(3340.1, 2095.5) * mm});
            skLineSegment(sketch, "E12.23.1.5", {"start": v(3213.1, 12.7) * mm, "end": v(3340.1, 12.7) * mm});
            skLineSegment(sketch, "E12.23.1.6", {"start": v(3340.1, 1041.4) * mm, "end": v(3213.1, 1041.4) * mm});
            skLineSegment(sketch, "E12.23.1.7", {"start": v(3340.1, 1066.8) * mm, "end": v(3213.1, 1066.8) * mm});
            skLineSegment(sketch, "E12.24.0.0", {"start": v(3352.8, 1041.4) * mm, "end": v(3352.8, 0) * mm});
            skLineSegment(sketch, "E12.24.0.1", {"start": v(3352.8, 1066.8) * mm, "end": v(3352.8, 2095.5) * mm});
            skLineSegment(sketch, "E12.24.0.2", {"start": v(3479.8, 12.7) * mm, "end": v(3479.8, 1041.4) * mm});
            skLineSegment(sketch, "E12.24.0.3", {"start": v(3479.8, 2095.5) * mm, "end": v(3479.8, 1066.8) * mm});
            skLineSegment(sketch, "E12.24.0.4", {"start": v(3352.8, 2095.5) * mm, "end": v(3479.8, 2095.5) * mm});
            skLineSegment(sketch, "E12.24.0.5", {"start": v(3352.8, 12.7) * mm, "end": v(3479.8, 12.7) * mm});
            skLineSegment(sketch, "E12.24.0.6", {"start": v(3479.8, 1041.4) * mm, "end": v(3352.8, 1041.4) * mm});
            skLineSegment(sketch, "E12.24.0.7", {"start": v(3479.8, 1066.8) * mm, "end": v(3352.8, 1066.8) * mm});
            skLineSegment(sketch, "E12.24.1.0", {"start": v(3352.8, 1041.4) * mm, "end": v(3352.8, 0) * mm});
            skLineSegment(sketch, "E12.24.1.1", {"start": v(3352.8, 1066.8) * mm, "end": v(3352.8, 2095.5) * mm});
            skLineSegment(sketch, "E12.24.1.2", {"start": v(3479.8, 12.7) * mm, "end": v(3479.8, 1041.4) * mm});
            skLineSegment(sketch, "E12.24.1.3", {"start": v(3479.8, 2095.5) * mm, "end": v(3479.8, 1066.8) * mm});
            skLineSegment(sketch, "E12.24.1.4", {"start": v(3352.8, 2095.5) * mm, "end": v(3479.8, 2095.5) * mm});
            skLineSegment(sketch, "E12.24.1.5", {"start": v(3352.8, 12.7) * mm, "end": v(3479.8, 12.7) * mm});
            skLineSegment(sketch, "E12.24.1.6", {"start": v(3479.8, 1041.4) * mm, "end": v(3352.8, 1041.4) * mm});
            skLineSegment(sketch, "E12.24.1.7", {"start": v(3479.8, 1066.8) * mm, "end": v(3352.8, 1066.8) * mm});
            skLineSegment(sketch, "E12.25.0.0", {"start": v(3492.5, 1041.4) * mm, "end": v(3492.5, 0) * mm});
            skLineSegment(sketch, "E12.25.0.1", {"start": v(3492.5, 1066.8) * mm, "end": v(3492.5, 2095.5) * mm});
            skLineSegment(sketch, "E12.25.0.2", {"start": v(3619.5, 12.7) * mm, "end": v(3619.5, 1041.4) * mm});
            skLineSegment(sketch, "E12.25.0.3", {"start": v(3619.5, 2095.5) * mm, "end": v(3619.5, 1066.8) * mm});
            skLineSegment(sketch, "E12.25.0.4", {"start": v(3492.5, 2095.5) * mm, "end": v(3619.5, 2095.5) * mm});
            skLineSegment(sketch, "E12.25.0.5", {"start": v(3492.5, 12.7) * mm, "end": v(3619.5, 12.7) * mm});
            skLineSegment(sketch, "E12.25.0.6", {"start": v(3619.5, 1041.4) * mm, "end": v(3492.5, 1041.4) * mm});
            skLineSegment(sketch, "E12.25.0.7", {"start": v(3619.5, 1066.8) * mm, "end": v(3492.5, 1066.8) * mm});
            skLineSegment(sketch, "E12.25.1.0", {"start": v(3492.5, 1041.4) * mm, "end": v(3492.5, 0) * mm});
            skLineSegment(sketch, "E12.25.1.1", {"start": v(3492.5, 1066.8) * mm, "end": v(3492.5, 2095.5) * mm});
            skLineSegment(sketch, "E12.25.1.2", {"start": v(3619.5, 12.7) * mm, "end": v(3619.5, 1041.4) * mm});
            skLineSegment(sketch, "E12.25.1.3", {"start": v(3619.5, 2095.5) * mm, "end": v(3619.5, 1066.8) * mm});
            skLineSegment(sketch, "E12.25.1.4", {"start": v(3492.5, 2095.5) * mm, "end": v(3619.5, 2095.5) * mm});
            skLineSegment(sketch, "E12.25.1.5", {"start": v(3492.5, 12.7) * mm, "end": v(3619.5, 12.7) * mm});
            skLineSegment(sketch, "E12.25.1.6", {"start": v(3619.5, 1041.4) * mm, "end": v(3492.5, 1041.4) * mm});
            skLineSegment(sketch, "E12.25.1.7", {"start": v(3619.5, 1066.8) * mm, "end": v(3492.5, 1066.8) * mm});
            skLineSegment(sketch, "E12.26.0.0", {"start": v(3632.2, 1041.4) * mm, "end": v(3632.2, 0) * mm});
            skLineSegment(sketch, "E12.26.0.1", {"start": v(3632.2, 1066.8) * mm, "end": v(3632.2, 2095.5) * mm});
            skLineSegment(sketch, "E12.26.0.2", {"start": v(3759.2, 12.7) * mm, "end": v(3759.2, 1041.4) * mm});
            skLineSegment(sketch, "E12.26.0.3", {"start": v(3759.2, 2095.5) * mm, "end": v(3759.2, 1066.8) * mm});
            skLineSegment(sketch, "E12.26.0.4", {"start": v(3632.2, 2095.5) * mm, "end": v(3759.2, 2095.5) * mm});
            skLineSegment(sketch, "E12.26.0.5", {"start": v(3632.2, 12.7) * mm, "end": v(3759.2, 12.7) * mm});
            skLineSegment(sketch, "E12.26.0.6", {"start": v(3759.2, 1041.4) * mm, "end": v(3632.2, 1041.4) * mm});
            skLineSegment(sketch, "E12.26.0.7", {"start": v(3759.2, 1066.8) * mm, "end": v(3632.2, 1066.8) * mm});
            skLineSegment(sketch, "E12.26.1.0", {"start": v(3632.2, 1041.4) * mm, "end": v(3632.2, 0) * mm});
            skLineSegment(sketch, "E12.26.1.1", {"start": v(3632.2, 1066.8) * mm, "end": v(3632.2, 2095.5) * mm});
            skLineSegment(sketch, "E12.26.1.2", {"start": v(3759.2, 12.7) * mm, "end": v(3759.2, 1041.4) * mm});
            skLineSegment(sketch, "E12.26.1.3", {"start": v(3759.2, 2095.5) * mm, "end": v(3759.2, 1066.8) * mm});
            skLineSegment(sketch, "E12.26.1.4", {"start": v(3632.2, 2095.5) * mm, "end": v(3759.2, 2095.5) * mm});
            skLineSegment(sketch, "E12.26.1.5", {"start": v(3632.2, 12.7) * mm, "end": v(3759.2, 12.7) * mm});
            skLineSegment(sketch, "E12.26.1.6", {"start": v(3759.2, 1041.4) * mm, "end": v(3632.2, 1041.4) * mm});
            skLineSegment(sketch, "E12.26.1.7", {"start": v(3759.2, 1066.8) * mm, "end": v(3632.2, 1066.8) * mm});
            skLineSegment(sketch, "E12.27.0.0", {"start": v(3771.9, 1041.4) * mm, "end": v(3771.9, 0) * mm});
            skLineSegment(sketch, "E12.27.0.1", {"start": v(3771.9, 1066.8) * mm, "end": v(3771.9, 2095.5) * mm});
            skLineSegment(sketch, "E12.27.0.2", {"start": v(3898.9, 12.7) * mm, "end": v(3898.9, 1041.4) * mm});
            skLineSegment(sketch, "E12.27.0.3", {"start": v(3898.9, 2095.5) * mm, "end": v(3898.9, 1066.8) * mm});
            skLineSegment(sketch, "E12.27.0.4", {"start": v(3771.9, 2095.5) * mm, "end": v(3898.9, 2095.5) * mm});
            skLineSegment(sketch, "E12.27.0.5", {"start": v(3771.9, 12.7) * mm, "end": v(3898.9, 12.7) * mm});
            skLineSegment(sketch, "E12.27.0.6", {"start": v(3898.9, 1041.4) * mm, "end": v(3771.9, 1041.4) * mm});
            skLineSegment(sketch, "E12.27.0.7", {"start": v(3898.9, 1066.8) * mm, "end": v(3771.9, 1066.8) * mm});
            skLineSegment(sketch, "E12.27.1.0", {"start": v(3771.9, 1041.4) * mm, "end": v(3771.9, 0) * mm});
            skLineSegment(sketch, "E12.27.1.1", {"start": v(3771.9, 1066.8) * mm, "end": v(3771.9, 2095.5) * mm});
            skLineSegment(sketch, "E12.27.1.2", {"start": v(3898.9, 12.7) * mm, "end": v(3898.9, 1041.4) * mm});
            skLineSegment(sketch, "E12.27.1.3", {"start": v(3898.9, 2095.5) * mm, "end": v(3898.9, 1066.8) * mm});
            skLineSegment(sketch, "E12.27.1.4", {"start": v(3771.9, 2095.5) * mm, "end": v(3898.9, 2095.5) * mm});
            skLineSegment(sketch, "E12.27.1.5", {"start": v(3771.9, 12.7) * mm, "end": v(3898.9, 12.7) * mm});
            skLineSegment(sketch, "E12.27.1.6", {"start": v(3898.9, 1041.4) * mm, "end": v(3771.9, 1041.4) * mm});
            skLineSegment(sketch, "E12.27.1.7", {"start": v(3898.9, 1066.8) * mm, "end": v(3771.9, 1066.8) * mm});
            skLineSegment(sketch, "E12.28.0.0", {"start": v(3911.6, 1041.4) * mm, "end": v(3911.6, 0) * mm});
            skLineSegment(sketch, "E12.28.0.1", {"start": v(3911.6, 1066.8) * mm, "end": v(3911.6, 2095.5) * mm});
            skLineSegment(sketch, "E12.28.0.2", {"start": v(4038.6, 12.7) * mm, "end": v(4038.6, 1041.4) * mm});
            skLineSegment(sketch, "E12.28.0.3", {"start": v(4038.6, 2095.5) * mm, "end": v(4038.6, 1066.8) * mm});
            skLineSegment(sketch, "E12.28.0.4", {"start": v(3911.6, 2095.5) * mm, "end": v(4038.6, 2095.5) * mm});
            skLineSegment(sketch, "E12.28.0.5", {"start": v(3911.6, 12.7) * mm, "end": v(4038.6, 12.7) * mm});
            skLineSegment(sketch, "E12.28.0.6", {"start": v(4038.6, 1041.4) * mm, "end": v(3911.6, 1041.4) * mm});
            skLineSegment(sketch, "E12.28.0.7", {"start": v(4038.6, 1066.8) * mm, "end": v(3911.6, 1066.8) * mm});
            skLineSegment(sketch, "E12.28.1.0", {"start": v(3911.6, 1041.4) * mm, "end": v(3911.6, 0) * mm});
            skLineSegment(sketch, "E12.28.1.1", {"start": v(3911.6, 1066.8) * mm, "end": v(3911.6, 2095.5) * mm});
            skLineSegment(sketch, "E12.28.1.2", {"start": v(4038.6, 12.7) * mm, "end": v(4038.6, 1041.4) * mm});
            skLineSegment(sketch, "E12.28.1.3", {"start": v(4038.6, 2095.5) * mm, "end": v(4038.6, 1066.8) * mm});
            skLineSegment(sketch, "E12.28.1.4", {"start": v(3911.6, 2095.5) * mm, "end": v(4038.6, 2095.5) * mm});
            skLineSegment(sketch, "E12.28.1.5", {"start": v(3911.6, 12.7) * mm, "end": v(4038.6, 12.7) * mm});
            skLineSegment(sketch, "E12.28.1.6", {"start": v(4038.6, 1041.4) * mm, "end": v(3911.6, 1041.4) * mm});
            skLineSegment(sketch, "E12.28.1.7", {"start": v(4038.6, 1066.8) * mm, "end": v(3911.6, 1066.8) * mm});
            skLineSegment(sketch, "E12.29.0.0", {"start": v(4051.3, 1041.4) * mm, "end": v(4051.3, 0) * mm});
            skLineSegment(sketch, "E12.29.0.1", {"start": v(4051.3, 1066.8) * mm, "end": v(4051.3, 2095.5) * mm});
            skLineSegment(sketch, "E12.29.0.2", {"start": v(4178.3, 12.7) * mm, "end": v(4178.3, 1041.4) * mm});
            skLineSegment(sketch, "E12.29.0.3", {"start": v(4178.3, 2095.5) * mm, "end": v(4178.3, 1066.8) * mm});
            skLineSegment(sketch, "E12.29.0.4", {"start": v(4051.3, 2095.5) * mm, "end": v(4178.3, 2095.5) * mm});
            skLineSegment(sketch, "E12.29.0.5", {"start": v(4051.3, 12.7) * mm, "end": v(4178.3, 12.7) * mm});
            skLineSegment(sketch, "E12.29.0.6", {"start": v(4178.3, 1041.4) * mm, "end": v(4051.3, 1041.4) * mm});
            skLineSegment(sketch, "E12.29.0.7", {"start": v(4178.3, 1066.8) * mm, "end": v(4051.3, 1066.8) * mm});
            skLineSegment(sketch, "E12.29.1.0", {"start": v(4051.3, 1041.4) * mm, "end": v(4051.3, 0) * mm});
            skLineSegment(sketch, "E12.29.1.1", {"start": v(4051.3, 1066.8) * mm, "end": v(4051.3, 2095.5) * mm});
            skLineSegment(sketch, "E12.29.1.2", {"start": v(4178.3, 12.7) * mm, "end": v(4178.3, 1041.4) * mm});
            skLineSegment(sketch, "E12.29.1.3", {"start": v(4178.3, 2095.5) * mm, "end": v(4178.3, 1066.8) * mm});
            skLineSegment(sketch, "E12.29.1.4", {"start": v(4051.3, 2095.5) * mm, "end": v(4178.3, 2095.5) * mm});
            skLineSegment(sketch, "E12.29.1.5", {"start": v(4051.3, 12.7) * mm, "end": v(4178.3, 12.7) * mm});
            skLineSegment(sketch, "E12.29.1.6", {"start": v(4178.3, 1041.4) * mm, "end": v(4051.3, 1041.4) * mm});
            skLineSegment(sketch, "E12.29.1.7", {"start": v(4178.3, 1066.8) * mm, "end": v(4051.3, 1066.8) * mm});
            skLineSegment(sketch, "E12.30.0.0", {"start": v(4191, 1041.4) * mm, "end": v(4191, 0) * mm});
            skLineSegment(sketch, "E12.30.0.1", {"start": v(4191, 1066.8) * mm, "end": v(4191, 2095.5) * mm});
            skLineSegment(sketch, "E12.30.0.2", {"start": v(4318, 12.7) * mm, "end": v(4318, 1041.4) * mm});
            skLineSegment(sketch, "E12.30.0.3", {"start": v(4318, 2095.5) * mm, "end": v(4318, 1066.8) * mm});
            skLineSegment(sketch, "E12.30.0.4", {"start": v(4191, 2095.5) * mm, "end": v(4318, 2095.5) * mm});
            skLineSegment(sketch, "E12.30.0.5", {"start": v(4191, 12.7) * mm, "end": v(4318, 12.7) * mm});
            skLineSegment(sketch, "E12.30.0.6", {"start": v(4318, 1041.4) * mm, "end": v(4191, 1041.4) * mm});
            skLineSegment(sketch, "E12.30.0.7", {"start": v(4318, 1066.8) * mm, "end": v(4191, 1066.8) * mm});
            skLineSegment(sketch, "E12.30.1.0", {"start": v(4191, 1041.4) * mm, "end": v(4191, 0) * mm});
            skLineSegment(sketch, "E12.30.1.1", {"start": v(4191, 1066.8) * mm, "end": v(4191, 2095.5) * mm});
            skLineSegment(sketch, "E12.30.1.2", {"start": v(4318, 12.7) * mm, "end": v(4318, 1041.4) * mm});
            skLineSegment(sketch, "E12.30.1.3", {"start": v(4318, 2095.5) * mm, "end": v(4318, 1066.8) * mm});
            skLineSegment(sketch, "E12.30.1.4", {"start": v(4191, 2095.5) * mm, "end": v(4318, 2095.5) * mm});
            skLineSegment(sketch, "E12.30.1.5", {"start": v(4191, 12.7) * mm, "end": v(4318, 12.7) * mm});
            skLineSegment(sketch, "E12.30.1.6", {"start": v(4318, 1041.4) * mm, "end": v(4191, 1041.4) * mm});
            skLineSegment(sketch, "E12.30.1.7", {"start": v(4318, 1066.8) * mm, "end": v(4191, 1066.8) * mm});
            skLineSegment(sketch, "E12.31.0.0", {"start": v(4330.7, 1041.4) * mm, "end": v(4330.7, 0) * mm});
            skLineSegment(sketch, "E12.31.0.1", {"start": v(4330.7, 1066.8) * mm, "end": v(4330.7, 2095.5) * mm});
            skLineSegment(sketch, "E12.31.0.2", {"start": v(4457.7, 12.7) * mm, "end": v(4457.7, 1041.4) * mm});
            skLineSegment(sketch, "E12.31.0.3", {"start": v(4457.7, 2095.5) * mm, "end": v(4457.7, 1066.8) * mm});
            skLineSegment(sketch, "E12.31.0.4", {"start": v(4330.7, 2095.5) * mm, "end": v(4457.7, 2095.5) * mm});
            skLineSegment(sketch, "E12.31.0.5", {"start": v(4330.7, 12.7) * mm, "end": v(4457.7, 12.7) * mm});
            skLineSegment(sketch, "E12.31.0.6", {"start": v(4457.7, 1041.4) * mm, "end": v(4330.7, 1041.4) * mm});
            skLineSegment(sketch, "E12.31.0.7", {"start": v(4457.7, 1066.8) * mm, "end": v(4330.7, 1066.8) * mm});
            skLineSegment(sketch, "E12.31.1.0", {"start": v(4330.7, 1041.4) * mm, "end": v(4330.7, 0) * mm});
            skLineSegment(sketch, "E12.31.1.1", {"start": v(4330.7, 1066.8) * mm, "end": v(4330.7, 2095.5) * mm});
            skLineSegment(sketch, "E12.31.1.2", {"start": v(4457.7, 12.7) * mm, "end": v(4457.7, 1041.4) * mm});
            skLineSegment(sketch, "E12.31.1.3", {"start": v(4457.7, 2095.5) * mm, "end": v(4457.7, 1066.8) * mm});
            skLineSegment(sketch, "E12.31.1.4", {"start": v(4330.7, 2095.5) * mm, "end": v(4457.7, 2095.5) * mm});
            skLineSegment(sketch, "E12.31.1.5", {"start": v(4330.7, 12.7) * mm, "end": v(4457.7, 12.7) * mm});
            skLineSegment(sketch, "E12.31.1.6", {"start": v(4457.7, 1041.4) * mm, "end": v(4330.7, 1041.4) * mm});
            skLineSegment(sketch, "E12.31.1.7", {"start": v(4457.7, 1066.8) * mm, "end": v(4330.7, 1066.8) * mm});
            skLineSegment(sketch, "E12.32.0.0", {"start": v(4470.4, 1041.4) * mm, "end": v(4470.4, 0) * mm});
            skLineSegment(sketch, "E12.32.0.1", {"start": v(4470.4, 1066.8) * mm, "end": v(4470.4, 2095.5) * mm});
            skLineSegment(sketch, "E12.32.0.2", {"start": v(4597.4, 12.7) * mm, "end": v(4597.4, 1041.4) * mm});
            skLineSegment(sketch, "E12.32.0.3", {"start": v(4597.4, 2095.5) * mm, "end": v(4597.4, 1066.8) * mm});
            skLineSegment(sketch, "E12.32.0.4", {"start": v(4470.4, 2095.5) * mm, "end": v(4597.4, 2095.5) * mm});
            skLineSegment(sketch, "E12.32.0.5", {"start": v(4470.4, 12.7) * mm, "end": v(4597.4, 12.7) * mm});
            skLineSegment(sketch, "E12.32.0.6", {"start": v(4597.4, 1041.4) * mm, "end": v(4470.4, 1041.4) * mm});
            skLineSegment(sketch, "E12.32.0.7", {"start": v(4597.4, 1066.8) * mm, "end": v(4470.4, 1066.8) * mm});
            skLineSegment(sketch, "E12.32.1.0", {"start": v(4470.4, 1041.4) * mm, "end": v(4470.4, 0) * mm});
            skLineSegment(sketch, "E12.32.1.1", {"start": v(4470.4, 1066.8) * mm, "end": v(4470.4, 2095.5) * mm});
            skLineSegment(sketch, "E12.32.1.2", {"start": v(4597.4, 12.7) * mm, "end": v(4597.4, 1041.4) * mm});
            skLineSegment(sketch, "E12.32.1.3", {"start": v(4597.4, 2095.5) * mm, "end": v(4597.4, 1066.8) * mm});
            skLineSegment(sketch, "E12.32.1.4", {"start": v(4470.4, 2095.5) * mm, "end": v(4597.4, 2095.5) * mm});
            skLineSegment(sketch, "E12.32.1.5", {"start": v(4470.4, 12.7) * mm, "end": v(4597.4, 12.7) * mm});
            skLineSegment(sketch, "E12.32.1.6", {"start": v(4597.4, 1041.4) * mm, "end": v(4470.4, 1041.4) * mm});
            skLineSegment(sketch, "E12.32.1.7", {"start": v(4597.4, 1066.8) * mm, "end": v(4470.4, 1066.8) * mm});
            skLineSegment(sketch, "E12.33.0.0", {"start": v(4610.1, 1041.4) * mm, "end": v(4610.1, 0) * mm});
            skLineSegment(sketch, "E12.33.0.1", {"start": v(4610.1, 1066.8) * mm, "end": v(4610.1, 2095.5) * mm});
            skLineSegment(sketch, "E12.33.0.2", {"start": v(4737.1, 12.7) * mm, "end": v(4737.1, 1041.4) * mm});
            skLineSegment(sketch, "E12.33.0.3", {"start": v(4737.1, 2095.5) * mm, "end": v(4737.1, 1066.8) * mm});
            skLineSegment(sketch, "E12.33.0.4", {"start": v(4610.1, 2095.5) * mm, "end": v(4737.1, 2095.5) * mm});
            skLineSegment(sketch, "E12.33.0.5", {"start": v(4610.1, 12.7) * mm, "end": v(4737.1, 12.7) * mm});
            skLineSegment(sketch, "E12.33.0.6", {"start": v(4737.1, 1041.4) * mm, "end": v(4610.1, 1041.4) * mm});
            skLineSegment(sketch, "E12.33.0.7", {"start": v(4737.1, 1066.8) * mm, "end": v(4610.1, 1066.8) * mm});
            skLineSegment(sketch, "E12.33.1.0", {"start": v(4610.1, 1041.4) * mm, "end": v(4610.1, 0) * mm});
            skLineSegment(sketch, "E12.33.1.1", {"start": v(4610.1, 1066.8) * mm, "end": v(4610.1, 2095.5) * mm});
            skLineSegment(sketch, "E12.33.1.2", {"start": v(4737.1, 12.7) * mm, "end": v(4737.1, 1041.4) * mm});
            skLineSegment(sketch, "E12.33.1.3", {"start": v(4737.1, 2095.5) * mm, "end": v(4737.1, 1066.8) * mm});
            skLineSegment(sketch, "E12.33.1.4", {"start": v(4610.1, 2095.5) * mm, "end": v(4737.1, 2095.5) * mm});
            skLineSegment(sketch, "E12.33.1.5", {"start": v(4610.1, 12.7) * mm, "end": v(4737.1, 12.7) * mm});
            skLineSegment(sketch, "E12.33.1.6", {"start": v(4737.1, 1041.4) * mm, "end": v(4610.1, 1041.4) * mm});
            skLineSegment(sketch, "E12.33.1.7", {"start": v(4737.1, 1066.8) * mm, "end": v(4610.1, 1066.8) * mm});
            skLineSegment(sketch, "E12.34.0.0", {"start": v(4749.8, 1041.4) * mm, "end": v(4749.8, 0) * mm});
            skLineSegment(sketch, "E12.34.0.1", {"start": v(4749.8, 1066.8) * mm, "end": v(4749.8, 2095.5) * mm});
            skLineSegment(sketch, "E12.34.0.2", {"start": v(4876.8, 12.7) * mm, "end": v(4876.8, 1041.4) * mm});
            skLineSegment(sketch, "E12.34.0.3", {"start": v(4876.8, 2095.5) * mm, "end": v(4876.8, 1066.8) * mm});
            skLineSegment(sketch, "E12.34.0.4", {"start": v(4749.8, 2095.5) * mm, "end": v(4876.8, 2095.5) * mm});
            skLineSegment(sketch, "E12.34.0.5", {"start": v(4749.8, 12.7) * mm, "end": v(4876.8, 12.7) * mm});
            skLineSegment(sketch, "E12.34.0.6", {"start": v(4876.8, 1041.4) * mm, "end": v(4749.8, 1041.4) * mm});
            skLineSegment(sketch, "E12.34.0.7", {"start": v(4876.8, 1066.8) * mm, "end": v(4749.8, 1066.8) * mm});
            skLineSegment(sketch, "E12.34.1.0", {"start": v(4749.8, 1041.4) * mm, "end": v(4749.8, 0) * mm});
            skLineSegment(sketch, "E12.34.1.1", {"start": v(4749.8, 1066.8) * mm, "end": v(4749.8, 2095.5) * mm});
            skLineSegment(sketch, "E12.34.1.2", {"start": v(4876.8, 12.7) * mm, "end": v(4876.8, 1041.4) * mm});
            skLineSegment(sketch, "E12.34.1.3", {"start": v(4876.8, 2095.5) * mm, "end": v(4876.8, 1066.8) * mm});
            skLineSegment(sketch, "E12.34.1.4", {"start": v(4749.8, 2095.5) * mm, "end": v(4876.8, 2095.5) * mm});
            skLineSegment(sketch, "E12.34.1.5", {"start": v(4749.8, 12.7) * mm, "end": v(4876.8, 12.7) * mm});
            skLineSegment(sketch, "E12.34.1.6", {"start": v(4876.8, 1041.4) * mm, "end": v(4749.8, 1041.4) * mm});
            skLineSegment(sketch, "E12.34.1.7", {"start": v(4876.8, 1066.8) * mm, "end": v(4749.8, 1066.8) * mm});
            skLineSegment(sketch, "E12.35.0.0", {"start": v(4889.5, 1041.4) * mm, "end": v(4889.5, 0) * mm});
            skLineSegment(sketch, "E12.35.0.1", {"start": v(4889.5, 1066.8) * mm, "end": v(4889.5, 2095.5) * mm});
            skLineSegment(sketch, "E12.35.0.2", {"start": v(5016.5, 12.7) * mm, "end": v(5016.5, 1041.4) * mm});
            skLineSegment(sketch, "E12.35.0.3", {"start": v(5016.5, 2095.5) * mm, "end": v(5016.5, 1066.8) * mm});
            skLineSegment(sketch, "E12.35.0.4", {"start": v(4889.5, 2095.5) * mm, "end": v(5016.5, 2095.5) * mm});
            skLineSegment(sketch, "E12.35.0.5", {"start": v(4889.5, 12.7) * mm, "end": v(5016.5, 12.7) * mm});
            skLineSegment(sketch, "E12.35.0.6", {"start": v(5016.5, 1041.4) * mm, "end": v(4889.5, 1041.4) * mm});
            skLineSegment(sketch, "E12.35.0.7", {"start": v(5016.5, 1066.8) * mm, "end": v(4889.5, 1066.8) * mm});
            skLineSegment(sketch, "E12.35.1.0", {"start": v(4889.5, 1041.4) * mm, "end": v(4889.5, 0) * mm});
            skLineSegment(sketch, "E12.35.1.1", {"start": v(4889.5, 1066.8) * mm, "end": v(4889.5, 2095.5) * mm});
            skLineSegment(sketch, "E12.35.1.2", {"start": v(5016.5, 12.7) * mm, "end": v(5016.5, 1041.4) * mm});
            skLineSegment(sketch, "E12.35.1.3", {"start": v(5016.5, 2095.5) * mm, "end": v(5016.5, 1066.8) * mm});
            skLineSegment(sketch, "E12.35.1.4", {"start": v(4889.5, 2095.5) * mm, "end": v(5016.5, 2095.5) * mm});
            skLineSegment(sketch, "E12.35.1.5", {"start": v(4889.5, 12.7) * mm, "end": v(5016.5, 12.7) * mm});
            skLineSegment(sketch, "E12.35.1.6", {"start": v(5016.5, 1041.4) * mm, "end": v(4889.5, 1041.4) * mm});
            skLineSegment(sketch, "E12.35.1.7", {"start": v(5016.5, 1066.8) * mm, "end": v(4889.5, 1066.8) * mm});
            skLineSegment(sketch, "E12.36.0.0", {"start": v(5029.2, 1041.4) * mm, "end": v(5029.2, 0) * mm});
            skLineSegment(sketch, "E12.36.0.1", {"start": v(5029.2, 1066.8) * mm, "end": v(5029.2, 2095.5) * mm});
            skLineSegment(sketch, "E12.36.0.2", {"start": v(5156.2, 12.7) * mm, "end": v(5156.2, 1041.4) * mm});
            skLineSegment(sketch, "E12.36.0.3", {"start": v(5156.2, 2095.5) * mm, "end": v(5156.2, 1066.8) * mm});
            skLineSegment(sketch, "E12.36.0.4", {"start": v(5029.2, 2095.5) * mm, "end": v(5156.2, 2095.5) * mm});
            skLineSegment(sketch, "E12.36.0.5", {"start": v(5029.2, 12.7) * mm, "end": v(5156.2, 12.7) * mm});
            skLineSegment(sketch, "E12.36.0.6", {"start": v(5156.2, 1041.4) * mm, "end": v(5029.2, 1041.4) * mm});
            skLineSegment(sketch, "E12.36.0.7", {"start": v(5156.2, 1066.8) * mm, "end": v(5029.2, 1066.8) * mm});
            skLineSegment(sketch, "E12.36.1.0", {"start": v(5029.2, 1041.4) * mm, "end": v(5029.2, 0) * mm});
            skLineSegment(sketch, "E12.36.1.1", {"start": v(5029.2, 1066.8) * mm, "end": v(5029.2, 2095.5) * mm});
            skLineSegment(sketch, "E12.36.1.2", {"start": v(5156.2, 12.7) * mm, "end": v(5156.2, 1041.4) * mm});
            skLineSegment(sketch, "E12.36.1.3", {"start": v(5156.2, 2095.5) * mm, "end": v(5156.2, 1066.8) * mm});
            skLineSegment(sketch, "E12.36.1.4", {"start": v(5029.2, 2095.5) * mm, "end": v(5156.2, 2095.5) * mm});
            skLineSegment(sketch, "E12.36.1.5", {"start": v(5029.2, 12.7) * mm, "end": v(5156.2, 12.7) * mm});
            skLineSegment(sketch, "E12.36.1.6", {"start": v(5156.2, 1041.4) * mm, "end": v(5029.2, 1041.4) * mm});
            skLineSegment(sketch, "E12.36.1.7", {"start": v(5156.2, 1066.8) * mm, "end": v(5029.2, 1066.8) * mm});
            skLineSegment(sketch, "E12.37.0.0", {"start": v(5168.9, 1041.4) * mm, "end": v(5168.9, 0) * mm});
            skLineSegment(sketch, "E12.37.0.1", {"start": v(5168.9, 1066.8) * mm, "end": v(5168.9, 2095.5) * mm});
            skLineSegment(sketch, "E12.37.0.2", {"start": v(5295.9, 12.7) * mm, "end": v(5295.9, 1041.4) * mm});
            skLineSegment(sketch, "E12.37.0.3", {"start": v(5295.9, 2095.5) * mm, "end": v(5295.9, 1066.8) * mm});
            skLineSegment(sketch, "E12.37.0.4", {"start": v(5168.9, 2095.5) * mm, "end": v(5295.9, 2095.5) * mm});
            skLineSegment(sketch, "E12.37.0.5", {"start": v(5168.9, 12.7) * mm, "end": v(5295.9, 12.7) * mm});
            skLineSegment(sketch, "E12.37.0.6", {"start": v(5295.9, 1041.4) * mm, "end": v(5168.9, 1041.4) * mm});
            skLineSegment(sketch, "E12.37.0.7", {"start": v(5295.9, 1066.8) * mm, "end": v(5168.9, 1066.8) * mm});
            skLineSegment(sketch, "E12.37.1.0", {"start": v(5168.9, 1041.4) * mm, "end": v(5168.9, 0) * mm});
            skLineSegment(sketch, "E12.37.1.1", {"start": v(5168.9, 1066.8) * mm, "end": v(5168.9, 2095.5) * mm});
            skLineSegment(sketch, "E12.37.1.2", {"start": v(5295.9, 12.7) * mm, "end": v(5295.9, 1041.4) * mm});
            skLineSegment(sketch, "E12.37.1.3", {"start": v(5295.9, 2095.5) * mm, "end": v(5295.9, 1066.8) * mm});
            skLineSegment(sketch, "E12.37.1.4", {"start": v(5168.9, 2095.5) * mm, "end": v(5295.9, 2095.5) * mm});
            skLineSegment(sketch, "E12.37.1.5", {"start": v(5168.9, 12.7) * mm, "end": v(5295.9, 12.7) * mm});
            skLineSegment(sketch, "E12.37.1.6", {"start": v(5295.9, 1041.4) * mm, "end": v(5168.9, 1041.4) * mm});
            skLineSegment(sketch, "E12.37.1.7", {"start": v(5295.9, 1066.8) * mm, "end": v(5168.9, 1066.8) * mm});
            skLineSegment(sketch, "E12.38.0.0", {"start": v(5308.6, 1041.4) * mm, "end": v(5308.6, 0) * mm});
            skLineSegment(sketch, "E12.38.0.1", {"start": v(5308.6, 1066.8) * mm, "end": v(5308.6, 2095.5) * mm});
            skLineSegment(sketch, "E12.38.0.2", {"start": v(5435.6, 12.7) * mm, "end": v(5435.6, 1041.4) * mm});
            skLineSegment(sketch, "E12.38.0.3", {"start": v(5435.6, 2095.5) * mm, "end": v(5435.6, 1066.8) * mm});
            skLineSegment(sketch, "E12.38.0.4", {"start": v(5308.6, 2095.5) * mm, "end": v(5435.6, 2095.5) * mm});
            skLineSegment(sketch, "E12.38.0.5", {"start": v(5308.6, 12.7) * mm, "end": v(5435.6, 12.7) * mm});
            skLineSegment(sketch, "E12.38.0.6", {"start": v(5435.6, 1041.4) * mm, "end": v(5308.6, 1041.4) * mm});
            skLineSegment(sketch, "E12.38.0.7", {"start": v(5435.6, 1066.8) * mm, "end": v(5308.6, 1066.8) * mm});
            skLineSegment(sketch, "E12.38.1.0", {"start": v(5308.6, 1041.4) * mm, "end": v(5308.6, 0) * mm});
            skLineSegment(sketch, "E12.38.1.1", {"start": v(5308.6, 1066.8) * mm, "end": v(5308.6, 2095.5) * mm});
            skLineSegment(sketch, "E12.38.1.2", {"start": v(5435.6, 12.7) * mm, "end": v(5435.6, 1041.4) * mm});
            skLineSegment(sketch, "E12.38.1.3", {"start": v(5435.6, 2095.5) * mm, "end": v(5435.6, 1066.8) * mm});
            skLineSegment(sketch, "E12.38.1.4", {"start": v(5308.6, 2095.5) * mm, "end": v(5435.6, 2095.5) * mm});
            skLineSegment(sketch, "E12.38.1.5", {"start": v(5308.6, 12.7) * mm, "end": v(5435.6, 12.7) * mm});
            skLineSegment(sketch, "E12.38.1.6", {"start": v(5435.6, 1041.4) * mm, "end": v(5308.6, 1041.4) * mm});
            skLineSegment(sketch, "E12.38.1.7", {"start": v(5435.6, 1066.8) * mm, "end": v(5308.6, 1066.8) * mm});
            skLineSegment(sketch, "E12.39.0.0", {"start": v(5448.3, 1041.4) * mm, "end": v(5448.3, 0) * mm});
            skLineSegment(sketch, "E12.39.0.1", {"start": v(5448.3, 1066.8) * mm, "end": v(5448.3, 2095.5) * mm});
            skLineSegment(sketch, "E12.39.0.2", {"start": v(5575.3, 12.7) * mm, "end": v(5575.3, 1041.4) * mm});
            skLineSegment(sketch, "E12.39.0.3", {"start": v(5575.3, 2095.5) * mm, "end": v(5575.3, 1066.8) * mm});
            skLineSegment(sketch, "E12.39.0.4", {"start": v(5448.3, 2095.5) * mm, "end": v(5575.3, 2095.5) * mm});
            skLineSegment(sketch, "E12.39.0.5", {"start": v(5448.3, 12.7) * mm, "end": v(5575.3, 12.7) * mm});
            skLineSegment(sketch, "E12.39.0.6", {"start": v(5575.3, 1041.4) * mm, "end": v(5448.3, 1041.4) * mm});
            skLineSegment(sketch, "E12.39.0.7", {"start": v(5575.3, 1066.8) * mm, "end": v(5448.3, 1066.8) * mm});
            skLineSegment(sketch, "E12.39.1.0", {"start": v(5448.3, 1041.4) * mm, "end": v(5448.3, 0) * mm});
            skLineSegment(sketch, "E12.39.1.1", {"start": v(5448.3, 1066.8) * mm, "end": v(5448.3, 2095.5) * mm});
            skLineSegment(sketch, "E12.39.1.2", {"start": v(5575.3, 12.7) * mm, "end": v(5575.3, 1041.4) * mm});
            skLineSegment(sketch, "E12.39.1.3", {"start": v(5575.3, 2095.5) * mm, "end": v(5575.3, 1066.8) * mm});
            skLineSegment(sketch, "E12.39.1.4", {"start": v(5448.3, 2095.5) * mm, "end": v(5575.3, 2095.5) * mm});
            skLineSegment(sketch, "E12.39.1.5", {"start": v(5448.3, 12.7) * mm, "end": v(5575.3, 12.7) * mm});
            skLineSegment(sketch, "E12.39.1.6", {"start": v(5575.3, 1041.4) * mm, "end": v(5448.3, 1041.4) * mm});
            skLineSegment(sketch, "E12.39.1.7", {"start": v(5575.3, 1066.8) * mm, "end": v(5448.3, 1066.8) * mm});
            skLineSegment(sketch, "E12.40.0.0", {"start": v(5588, 1041.4) * mm, "end": v(5588, 0) * mm});
            skLineSegment(sketch, "E12.40.0.1", {"start": v(5588, 1066.8) * mm, "end": v(5588, 2095.5) * mm});
            skLineSegment(sketch, "E12.40.0.2", {"start": v(5715, 12.7) * mm, "end": v(5715, 1041.4) * mm});
            skLineSegment(sketch, "E12.40.0.3", {"start": v(5715, 2095.5) * mm, "end": v(5715, 1066.8) * mm});
            skLineSegment(sketch, "E12.40.0.4", {"start": v(5588, 2095.5) * mm, "end": v(5715, 2095.5) * mm});
            skLineSegment(sketch, "E12.40.0.5", {"start": v(5588, 12.7) * mm, "end": v(5715, 12.7) * mm});
            skLineSegment(sketch, "E12.40.0.6", {"start": v(5715, 1041.4) * mm, "end": v(5588, 1041.4) * mm});
            skLineSegment(sketch, "E12.40.0.7", {"start": v(5715, 1066.8) * mm, "end": v(5588, 1066.8) * mm});
            skLineSegment(sketch, "E12.40.1.0", {"start": v(5588, 1041.4) * mm, "end": v(5588, 0) * mm});
            skLineSegment(sketch, "E12.40.1.1", {"start": v(5588, 1066.8) * mm, "end": v(5588, 2095.5) * mm});
            skLineSegment(sketch, "E12.40.1.2", {"start": v(5715, 12.7) * mm, "end": v(5715, 1041.4) * mm});
            skLineSegment(sketch, "E12.40.1.3", {"start": v(5715, 2095.5) * mm, "end": v(5715, 1066.8) * mm});
            skLineSegment(sketch, "E12.40.1.4", {"start": v(5588, 2095.5) * mm, "end": v(5715, 2095.5) * mm});
            skLineSegment(sketch, "E12.40.1.5", {"start": v(5588, 12.7) * mm, "end": v(5715, 12.7) * mm});
            skLineSegment(sketch, "E12.40.1.6", {"start": v(5715, 1041.4) * mm, "end": v(5588, 1041.4) * mm});
            skLineSegment(sketch, "E12.40.1.7", {"start": v(5715, 1066.8) * mm, "end": v(5588, 1066.8) * mm});
            skLineSegment(sketch, "E12.41.0.0", {"start": v(5727.7, 1041.4) * mm, "end": v(5727.7, 0) * mm});
            skLineSegment(sketch, "E12.41.0.1", {"start": v(5727.7, 1066.8) * mm, "end": v(5727.7, 2095.5) * mm});
            skLineSegment(sketch, "E12.41.0.2", {"start": v(5854.7, 12.7) * mm, "end": v(5854.7, 1041.4) * mm});
            skLineSegment(sketch, "E12.41.0.3", {"start": v(5854.7, 2095.5) * mm, "end": v(5854.7, 1066.8) * mm});
            skLineSegment(sketch, "E12.41.0.4", {"start": v(5727.7, 2095.5) * mm, "end": v(5854.7, 2095.5) * mm});
            skLineSegment(sketch, "E12.41.0.5", {"start": v(5727.7, 12.7) * mm, "end": v(5854.7, 12.7) * mm});
            skLineSegment(sketch, "E12.41.0.6", {"start": v(5854.7, 1041.4) * mm, "end": v(5727.7, 1041.4) * mm});
            skLineSegment(sketch, "E12.41.0.7", {"start": v(5854.7, 1066.8) * mm, "end": v(5727.7, 1066.8) * mm});
            skLineSegment(sketch, "E12.41.1.0", {"start": v(5727.7, 1041.4) * mm, "end": v(5727.7, 0) * mm});
            skLineSegment(sketch, "E12.41.1.1", {"start": v(5727.7, 1066.8) * mm, "end": v(5727.7, 2095.5) * mm});
            skLineSegment(sketch, "E12.41.1.2", {"start": v(5854.7, 12.7) * mm, "end": v(5854.7, 1041.4) * mm});
            skLineSegment(sketch, "E12.41.1.3", {"start": v(5854.7, 2095.5) * mm, "end": v(5854.7, 1066.8) * mm});
            skLineSegment(sketch, "E12.41.1.4", {"start": v(5727.7, 2095.5) * mm, "end": v(5854.7, 2095.5) * mm});
            skLineSegment(sketch, "E12.41.1.5", {"start": v(5727.7, 12.7) * mm, "end": v(5854.7, 12.7) * mm});
            skLineSegment(sketch, "E12.41.1.6", {"start": v(5854.7, 1041.4) * mm, "end": v(5727.7, 1041.4) * mm});
            skLineSegment(sketch, "E12.41.1.7", {"start": v(5854.7, 1066.8) * mm, "end": v(5727.7, 1066.8) * mm});
            skLineSegment(sketch, "E12.42.0.0", {"start": v(5867.4, 1041.4) * mm, "end": v(5867.4, 0) * mm});
            skLineSegment(sketch, "E12.42.0.1", {"start": v(5867.4, 1066.8) * mm, "end": v(5867.4, 2095.5) * mm});
            skLineSegment(sketch, "E12.42.0.2", {"start": v(5994.4, 12.7) * mm, "end": v(5994.4, 1041.4) * mm});
            skLineSegment(sketch, "E12.42.0.3", {"start": v(5994.4, 2095.5) * mm, "end": v(5994.4, 1066.8) * mm});
            skLineSegment(sketch, "E12.42.0.4", {"start": v(5867.4, 2095.5) * mm, "end": v(5994.4, 2095.5) * mm});
            skLineSegment(sketch, "E12.42.0.5", {"start": v(5867.4, 12.7) * mm, "end": v(5994.4, 12.7) * mm});
            skLineSegment(sketch, "E12.42.0.6", {"start": v(5994.4, 1041.4) * mm, "end": v(5867.4, 1041.4) * mm});
            skLineSegment(sketch, "E12.42.0.7", {"start": v(5994.4, 1066.8) * mm, "end": v(5867.4, 1066.8) * mm});
            skLineSegment(sketch, "E12.42.1.0", {"start": v(5867.4, 1041.4) * mm, "end": v(5867.4, 0) * mm});
            skLineSegment(sketch, "E12.42.1.1", {"start": v(5867.4, 1066.8) * mm, "end": v(5867.4, 2095.5) * mm});
            skLineSegment(sketch, "E12.42.1.2", {"start": v(5994.4, 12.7) * mm, "end": v(5994.4, 1041.4) * mm});
            skLineSegment(sketch, "E12.42.1.3", {"start": v(5994.4, 2095.5) * mm, "end": v(5994.4, 1066.8) * mm});
            skLineSegment(sketch, "E12.42.1.4", {"start": v(5867.4, 2095.5) * mm, "end": v(5994.4, 2095.5) * mm});
            skLineSegment(sketch, "E12.42.1.5", {"start": v(5867.4, 12.7) * mm, "end": v(5994.4, 12.7) * mm});
            skLineSegment(sketch, "E12.42.1.6", {"start": v(5994.4, 1041.4) * mm, "end": v(5867.4, 1041.4) * mm});
            skLineSegment(sketch, "E12.42.1.7", {"start": v(5994.4, 1066.8) * mm, "end": v(5867.4, 1066.8) * mm});
            skLineSegment(sketch, "E12.43.0.0", {"start": v(6007.1, 1041.4) * mm, "end": v(6007.1, 0) * mm});
            skLineSegment(sketch, "E12.43.0.1", {"start": v(6007.1, 1066.8) * mm, "end": v(6007.1, 2095.5) * mm});
            skLineSegment(sketch, "E12.43.0.2", {"start": v(6134.1, 12.7) * mm, "end": v(6134.1, 1041.4) * mm});
            skLineSegment(sketch, "E12.43.0.3", {"start": v(6134.1, 2095.5) * mm, "end": v(6134.1, 1066.8) * mm});
            skLineSegment(sketch, "E12.43.0.4", {"start": v(6007.1, 2095.5) * mm, "end": v(6134.1, 2095.5) * mm});
            skLineSegment(sketch, "E12.43.0.5", {"start": v(6007.1, 12.7) * mm, "end": v(6134.1, 12.7) * mm});
            skLineSegment(sketch, "E12.43.0.6", {"start": v(6134.1, 1041.4) * mm, "end": v(6007.1, 1041.4) * mm});
            skLineSegment(sketch, "E12.43.0.7", {"start": v(6134.1, 1066.8) * mm, "end": v(6007.1, 1066.8) * mm});
            skLineSegment(sketch, "E12.43.1.0", {"start": v(6007.1, 1041.4) * mm, "end": v(6007.1, 0) * mm});
            skLineSegment(sketch, "E12.43.1.1", {"start": v(6007.1, 1066.8) * mm, "end": v(6007.1, 2095.5) * mm});
            skLineSegment(sketch, "E12.43.1.2", {"start": v(6134.1, 12.7) * mm, "end": v(6134.1, 1041.4) * mm});
            skLineSegment(sketch, "E12.43.1.3", {"start": v(6134.1, 2095.5) * mm, "end": v(6134.1, 1066.8) * mm});
            skLineSegment(sketch, "E12.43.1.4", {"start": v(6007.1, 2095.5) * mm, "end": v(6134.1, 2095.5) * mm});
            skLineSegment(sketch, "E12.43.1.5", {"start": v(6007.1, 12.7) * mm, "end": v(6134.1, 12.7) * mm});
            skLineSegment(sketch, "E12.43.1.6", {"start": v(6134.1, 1041.4) * mm, "end": v(6007.1, 1041.4) * mm});
            skLineSegment(sketch, "E12.43.1.7", {"start": v(6134.1, 1066.8) * mm, "end": v(6007.1, 1066.8) * mm});
            skLineSegment(sketch, "E12.44.0.0", {"start": v(6146.8, 1041.4) * mm, "end": v(6146.8, 0) * mm});
            skLineSegment(sketch, "E12.44.0.1", {"start": v(6146.8, 1066.8) * mm, "end": v(6146.8, 2095.5) * mm});
            skLineSegment(sketch, "E12.44.0.2", {"start": v(6273.8, 12.7) * mm, "end": v(6273.8, 1041.4) * mm});
            skLineSegment(sketch, "E12.44.0.3", {"start": v(6273.8, 2095.5) * mm, "end": v(6273.8, 1066.8) * mm});
            skLineSegment(sketch, "E12.44.0.4", {"start": v(6146.8, 2095.5) * mm, "end": v(6273.8, 2095.5) * mm});
            skLineSegment(sketch, "E12.44.0.5", {"start": v(6146.8, 12.7) * mm, "end": v(6273.8, 12.7) * mm});
            skLineSegment(sketch, "E12.44.0.6", {"start": v(6273.8, 1041.4) * mm, "end": v(6146.8, 1041.4) * mm});
            skLineSegment(sketch, "E12.44.0.7", {"start": v(6273.8, 1066.8) * mm, "end": v(6146.8, 1066.8) * mm});
            skLineSegment(sketch, "E12.44.1.0", {"start": v(6146.8, 1041.4) * mm, "end": v(6146.8, 0) * mm});
            skLineSegment(sketch, "E12.44.1.1", {"start": v(6146.8, 1066.8) * mm, "end": v(6146.8, 2095.5) * mm});
            skLineSegment(sketch, "E12.44.1.2", {"start": v(6273.8, 12.7) * mm, "end": v(6273.8, 1041.4) * mm});
            skLineSegment(sketch, "E12.44.1.3", {"start": v(6273.8, 2095.5) * mm, "end": v(6273.8, 1066.8) * mm});
            skLineSegment(sketch, "E12.44.1.4", {"start": v(6146.8, 2095.5) * mm, "end": v(6273.8, 2095.5) * mm});
            skLineSegment(sketch, "E12.44.1.5", {"start": v(6146.8, 12.7) * mm, "end": v(6273.8, 12.7) * mm});
            skLineSegment(sketch, "E12.44.1.6", {"start": v(6273.8, 1041.4) * mm, "end": v(6146.8, 1041.4) * mm});
            skLineSegment(sketch, "E12.44.1.7", {"start": v(6273.8, 1066.8) * mm, "end": v(6146.8, 1066.8) * mm});
            skLineSegment(sketch, "E12.45.0.0", {"start": v(6286.5, 1041.4) * mm, "end": v(6286.5, 0) * mm});
            skLineSegment(sketch, "E12.45.0.1", {"start": v(6286.5, 1066.8) * mm, "end": v(6286.5, 2095.5) * mm});
            skLineSegment(sketch, "E12.45.0.2", {"start": v(6413.5, 12.7) * mm, "end": v(6413.5, 1041.4) * mm});
            skLineSegment(sketch, "E12.45.0.3", {"start": v(6413.5, 2095.5) * mm, "end": v(6413.5, 1066.8) * mm});
            skLineSegment(sketch, "E12.45.0.4", {"start": v(6286.5, 2095.5) * mm, "end": v(6413.5, 2095.5) * mm});
            skLineSegment(sketch, "E12.45.0.5", {"start": v(6286.5, 12.7) * mm, "end": v(6413.5, 12.7) * mm});
            skLineSegment(sketch, "E12.45.0.6", {"start": v(6413.5, 1041.4) * mm, "end": v(6286.5, 1041.4) * mm});
            skLineSegment(sketch, "E12.45.0.7", {"start": v(6413.5, 1066.8) * mm, "end": v(6286.5, 1066.8) * mm});
            skLineSegment(sketch, "E12.45.1.0", {"start": v(6286.5, 1041.4) * mm, "end": v(6286.5, 0) * mm});
            skLineSegment(sketch, "E12.45.1.1", {"start": v(6286.5, 1066.8) * mm, "end": v(6286.5, 2095.5) * mm});
            skLineSegment(sketch, "E12.45.1.2", {"start": v(6413.5, 12.7) * mm, "end": v(6413.5, 1041.4) * mm});
            skLineSegment(sketch, "E12.45.1.3", {"start": v(6413.5, 2095.5) * mm, "end": v(6413.5, 1066.8) * mm});
            skLineSegment(sketch, "E12.45.1.4", {"start": v(6286.5, 2095.5) * mm, "end": v(6413.5, 2095.5) * mm});
            skLineSegment(sketch, "E12.45.1.5", {"start": v(6286.5, 12.7) * mm, "end": v(6413.5, 12.7) * mm});
            skLineSegment(sketch, "E12.45.1.6", {"start": v(6413.5, 1041.4) * mm, "end": v(6286.5, 1041.4) * mm});
            skLineSegment(sketch, "E12.45.1.7", {"start": v(6413.5, 1066.8) * mm, "end": v(6286.5, 1066.8) * mm});
            skLineSegment(sketch, "E12.46.0.0", {"start": v(6426.2, 1041.4) * mm, "end": v(6426.2, 0) * mm});
            skLineSegment(sketch, "E12.46.0.1", {"start": v(6426.2, 1066.8) * mm, "end": v(6426.2, 2095.5) * mm});
            skLineSegment(sketch, "E12.46.0.2", {"start": v(6553.2, 12.7) * mm, "end": v(6553.2, 1041.4) * mm});
            skLineSegment(sketch, "E12.46.0.3", {"start": v(6553.2, 2095.5) * mm, "end": v(6553.2, 1066.8) * mm});
            skLineSegment(sketch, "E12.46.0.4", {"start": v(6426.2, 2095.5) * mm, "end": v(6553.2, 2095.5) * mm});
            skLineSegment(sketch, "E12.46.0.5", {"start": v(6426.2, 12.7) * mm, "end": v(6553.2, 12.7) * mm});
            skLineSegment(sketch, "E12.46.0.6", {"start": v(6553.2, 1041.4) * mm, "end": v(6426.2, 1041.4) * mm});
            skLineSegment(sketch, "E12.46.0.7", {"start": v(6553.2, 1066.8) * mm, "end": v(6426.2, 1066.8) * mm});
            skLineSegment(sketch, "E12.46.1.0", {"start": v(6426.2, 1041.4) * mm, "end": v(6426.2, 0) * mm});
            skLineSegment(sketch, "E12.46.1.1", {"start": v(6426.2, 1066.8) * mm, "end": v(6426.2, 2095.5) * mm});
            skLineSegment(sketch, "E12.46.1.2", {"start": v(6553.2, 12.7) * mm, "end": v(6553.2, 1041.4) * mm});
            skLineSegment(sketch, "E12.46.1.3", {"start": v(6553.2, 2095.5) * mm, "end": v(6553.2, 1066.8) * mm});
            skLineSegment(sketch, "E12.46.1.4", {"start": v(6426.2, 2095.5) * mm, "end": v(6553.2, 2095.5) * mm});
            skLineSegment(sketch, "E12.46.1.5", {"start": v(6426.2, 12.7) * mm, "end": v(6553.2, 12.7) * mm});
            skLineSegment(sketch, "E12.46.1.6", {"start": v(6553.2, 1041.4) * mm, "end": v(6426.2, 1041.4) * mm});
            skLineSegment(sketch, "E12.46.1.7", {"start": v(6553.2, 1066.8) * mm, "end": v(6426.2, 1066.8) * mm});
            skLineSegment(sketch, "E12.47.0.0", {"start": v(6565.9, 1041.4) * mm, "end": v(6565.9, 0) * mm});
            skLineSegment(sketch, "E12.47.0.1", {"start": v(6565.9, 1066.8) * mm, "end": v(6565.9, 2095.5) * mm});
            skLineSegment(sketch, "E12.47.0.2", {"start": v(6692.9, 12.7) * mm, "end": v(6692.9, 1041.4) * mm});
            skLineSegment(sketch, "E12.47.0.3", {"start": v(6692.9, 2095.5) * mm, "end": v(6692.9, 1066.8) * mm});
            skLineSegment(sketch, "E12.47.0.4", {"start": v(6565.9, 2095.5) * mm, "end": v(6692.9, 2095.5) * mm});
            skLineSegment(sketch, "E12.47.0.5", {"start": v(6565.9, 12.7) * mm, "end": v(6692.9, 12.7) * mm});
            skLineSegment(sketch, "E12.47.0.6", {"start": v(6692.9, 1041.4) * mm, "end": v(6565.9, 1041.4) * mm});
            skLineSegment(sketch, "E12.47.0.7", {"start": v(6692.9, 1066.8) * mm, "end": v(6565.9, 1066.8) * mm});
            skLineSegment(sketch, "E12.47.1.0", {"start": v(6565.9, 1041.4) * mm, "end": v(6565.9, 0) * mm});
            skLineSegment(sketch, "E12.47.1.1", {"start": v(6565.9, 1066.8) * mm, "end": v(6565.9, 2095.5) * mm});
            skLineSegment(sketch, "E12.47.1.2", {"start": v(6692.9, 12.7) * mm, "end": v(6692.9, 1041.4) * mm});
            skLineSegment(sketch, "E12.47.1.3", {"start": v(6692.9, 2095.5) * mm, "end": v(6692.9, 1066.8) * mm});
            skLineSegment(sketch, "E12.47.1.4", {"start": v(6565.9, 2095.5) * mm, "end": v(6692.9, 2095.5) * mm});
            skLineSegment(sketch, "E12.47.1.5", {"start": v(6565.9, 12.7) * mm, "end": v(6692.9, 12.7) * mm});
            skLineSegment(sketch, "E12.47.1.6", {"start": v(6692.9, 1041.4) * mm, "end": v(6565.9, 1041.4) * mm});
            skLineSegment(sketch, "E12.47.1.7", {"start": v(6692.9, 1066.8) * mm, "end": v(6565.9, 1066.8) * mm});
            skLineSegment(sketch, "E12.48.0.0", {"start": v(6705.6, 1041.4) * mm, "end": v(6705.6, 0) * mm});
            skLineSegment(sketch, "E12.48.0.1", {"start": v(6705.6, 1066.8) * mm, "end": v(6705.6, 2095.5) * mm});
            skLineSegment(sketch, "E12.48.0.2", {"start": v(6832.6, 12.7) * mm, "end": v(6832.6, 1041.4) * mm});
            skLineSegment(sketch, "E12.48.0.3", {"start": v(6832.6, 2095.5) * mm, "end": v(6832.6, 1066.8) * mm});
            skLineSegment(sketch, "E12.48.0.4", {"start": v(6705.6, 2095.5) * mm, "end": v(6832.6, 2095.5) * mm});
            skLineSegment(sketch, "E12.48.0.5", {"start": v(6705.6, 12.7) * mm, "end": v(6832.6, 12.7) * mm});
            skLineSegment(sketch, "E12.48.0.6", {"start": v(6832.6, 1041.4) * mm, "end": v(6705.6, 1041.4) * mm});
            skLineSegment(sketch, "E12.48.0.7", {"start": v(6832.6, 1066.8) * mm, "end": v(6705.6, 1066.8) * mm});
            skLineSegment(sketch, "E12.48.1.0", {"start": v(6705.6, 1041.4) * mm, "end": v(6705.6, 0) * mm});
            skLineSegment(sketch, "E12.48.1.1", {"start": v(6705.6, 1066.8) * mm, "end": v(6705.6, 2095.5) * mm});
            skLineSegment(sketch, "E12.48.1.2", {"start": v(6832.6, 12.7) * mm, "end": v(6832.6, 1041.4) * mm});
            skLineSegment(sketch, "E12.48.1.3", {"start": v(6832.6, 2095.5) * mm, "end": v(6832.6, 1066.8) * mm});
            skLineSegment(sketch, "E12.48.1.4", {"start": v(6705.6, 2095.5) * mm, "end": v(6832.6, 2095.5) * mm});
            skLineSegment(sketch, "E12.48.1.5", {"start": v(6705.6, 12.7) * mm, "end": v(6832.6, 12.7) * mm});
            skLineSegment(sketch, "E12.48.1.6", {"start": v(6832.6, 1041.4) * mm, "end": v(6705.6, 1041.4) * mm});
            skLineSegment(sketch, "E12.48.1.7", {"start": v(6832.6, 1066.8) * mm, "end": v(6705.6, 1066.8) * mm});
            skLineSegment(sketch, "E12.49.0.0", {"start": v(6845.3, 1041.4) * mm, "end": v(6845.3, 0) * mm});
            skLineSegment(sketch, "E12.49.0.1", {"start": v(6845.3, 1066.8) * mm, "end": v(6845.3, 2095.5) * mm});
            skLineSegment(sketch, "E12.49.0.2", {"start": v(6972.3, 12.7) * mm, "end": v(6972.3, 1041.4) * mm});
            skLineSegment(sketch, "E12.49.0.3", {"start": v(6972.3, 2095.5) * mm, "end": v(6972.3, 1066.8) * mm});
            skLineSegment(sketch, "E12.49.0.4", {"start": v(6845.3, 2095.5) * mm, "end": v(6972.3, 2095.5) * mm});
            skLineSegment(sketch, "E12.49.0.5", {"start": v(6845.3, 12.7) * mm, "end": v(6972.3, 12.7) * mm});
            skLineSegment(sketch, "E12.49.0.6", {"start": v(6972.3, 1041.4) * mm, "end": v(6845.3, 1041.4) * mm});
            skLineSegment(sketch, "E12.49.0.7", {"start": v(6972.3, 1066.8) * mm, "end": v(6845.3, 1066.8) * mm});
            skLineSegment(sketch, "E12.49.1.0", {"start": v(6845.3, 1041.4) * mm, "end": v(6845.3, 0) * mm});
            skLineSegment(sketch, "E12.49.1.1", {"start": v(6845.3, 1066.8) * mm, "end": v(6845.3, 2095.5) * mm});
            skLineSegment(sketch, "E12.49.1.2", {"start": v(6972.3, 12.7) * mm, "end": v(6972.3, 1041.4) * mm});
            skLineSegment(sketch, "E12.49.1.3", {"start": v(6972.3, 2095.5) * mm, "end": v(6972.3, 1066.8) * mm});
            skLineSegment(sketch, "E12.49.1.4", {"start": v(6845.3, 2095.5) * mm, "end": v(6972.3, 2095.5) * mm});
            skLineSegment(sketch, "E12.49.1.5", {"start": v(6845.3, 12.7) * mm, "end": v(6972.3, 12.7) * mm});
            skLineSegment(sketch, "E12.49.1.6", {"start": v(6972.3, 1041.4) * mm, "end": v(6845.3, 1041.4) * mm});
            skLineSegment(sketch, "E12.49.1.7", {"start": v(6972.3, 1066.8) * mm, "end": v(6845.3, 1066.8) * mm});
            skLineSegment(sketch, "E12.50.0.0", {"start": v(6985, 1041.4) * mm, "end": v(6985, 0) * mm});
            skLineSegment(sketch, "E12.50.0.1", {"start": v(6985, 1066.8) * mm, "end": v(6985, 2095.5) * mm});
            skLineSegment(sketch, "E12.50.0.2", {"start": v(7112, 12.7) * mm, "end": v(7112, 1041.4) * mm});
            skLineSegment(sketch, "E12.50.0.3", {"start": v(7112, 2095.5) * mm, "end": v(7112, 1066.8) * mm});
            skLineSegment(sketch, "E12.50.0.4", {"start": v(6985, 2095.5) * mm, "end": v(7112, 2095.5) * mm});
            skLineSegment(sketch, "E12.50.0.5", {"start": v(6985, 12.7) * mm, "end": v(7112, 12.7) * mm});
            skLineSegment(sketch, "E12.50.0.6", {"start": v(7112, 1041.4) * mm, "end": v(6985, 1041.4) * mm});
            skLineSegment(sketch, "E12.50.0.7", {"start": v(7112, 1066.8) * mm, "end": v(6985, 1066.8) * mm});
            skLineSegment(sketch, "E12.50.1.0", {"start": v(6985, 1041.4) * mm, "end": v(6985, 0) * mm});
            skLineSegment(sketch, "E12.50.1.1", {"start": v(6985, 1066.8) * mm, "end": v(6985, 2095.5) * mm});
            skLineSegment(sketch, "E12.50.1.2", {"start": v(7112, 12.7) * mm, "end": v(7112, 1041.4) * mm});
            skLineSegment(sketch, "E12.50.1.3", {"start": v(7112, 2095.5) * mm, "end": v(7112, 1066.8) * mm});
            skLineSegment(sketch, "E12.50.1.4", {"start": v(6985, 2095.5) * mm, "end": v(7112, 2095.5) * mm});
            skLineSegment(sketch, "E12.50.1.5", {"start": v(6985, 12.7) * mm, "end": v(7112, 12.7) * mm});
            skLineSegment(sketch, "E12.50.1.6", {"start": v(7112, 1041.4) * mm, "end": v(6985, 1041.4) * mm});
            skLineSegment(sketch, "E12.50.1.7", {"start": v(7112, 1066.8) * mm, "end": v(6985, 1066.8) * mm});
            skLineSegment(sketch, "E12.51.0.0", {"start": v(7124.7, 1041.4) * mm, "end": v(7124.7, 0) * mm});
            skLineSegment(sketch, "E12.51.0.1", {"start": v(7124.7, 1066.8) * mm, "end": v(7124.7, 2095.5) * mm});
            skLineSegment(sketch, "E12.51.0.2", {"start": v(7251.7, 12.7) * mm, "end": v(7251.7, 1041.4) * mm});
            skLineSegment(sketch, "E12.51.0.3", {"start": v(7251.7, 2095.5) * mm, "end": v(7251.7, 1066.8) * mm});
            skLineSegment(sketch, "E12.51.0.4", {"start": v(7124.7, 2095.5) * mm, "end": v(7251.7, 2095.5) * mm});
            skLineSegment(sketch, "E12.51.0.5", {"start": v(7124.7, 12.7) * mm, "end": v(7251.7, 12.7) * mm});
            skLineSegment(sketch, "E12.51.0.6", {"start": v(7251.7, 1041.4) * mm, "end": v(7124.7, 1041.4) * mm});
            skLineSegment(sketch, "E12.51.0.7", {"start": v(7251.7, 1066.8) * mm, "end": v(7124.7, 1066.8) * mm});
            skLineSegment(sketch, "E12.51.1.0", {"start": v(7124.7, 1041.4) * mm, "end": v(7124.7, 0) * mm});
            skLineSegment(sketch, "E12.51.1.1", {"start": v(7124.7, 1066.8) * mm, "end": v(7124.7, 2095.5) * mm});
            skLineSegment(sketch, "E12.51.1.2", {"start": v(7251.7, 12.7) * mm, "end": v(7251.7, 1041.4) * mm});
            skLineSegment(sketch, "E12.51.1.3", {"start": v(7251.7, 2095.5) * mm, "end": v(7251.7, 1066.8) * mm});
            skLineSegment(sketch, "E12.51.1.4", {"start": v(7124.7, 2095.5) * mm, "end": v(7251.7, 2095.5) * mm});
            skLineSegment(sketch, "E12.51.1.5", {"start": v(7124.7, 12.7) * mm, "end": v(7251.7, 12.7) * mm});
            skLineSegment(sketch, "E12.51.1.6", {"start": v(7251.7, 1041.4) * mm, "end": v(7124.7, 1041.4) * mm});
            skLineSegment(sketch, "E12.51.1.7", {"start": v(7251.7, 1066.8) * mm, "end": v(7124.7, 1066.8) * mm});
            skLineSegment(sketch, "E12.52.0.0", {"start": v(7264.4, 1041.4) * mm, "end": v(7264.4, 0) * mm});
            skLineSegment(sketch, "E12.52.0.1", {"start": v(7264.4, 1066.8) * mm, "end": v(7264.4, 2095.5) * mm});
            skLineSegment(sketch, "E12.52.0.2", {"start": v(7391.4, 12.7) * mm, "end": v(7391.4, 1041.4) * mm});
            skLineSegment(sketch, "E12.52.0.3", {"start": v(7391.4, 2095.5) * mm, "end": v(7391.4, 1066.8) * mm});
            skLineSegment(sketch, "E12.52.0.4", {"start": v(7264.4, 2095.5) * mm, "end": v(7391.4, 2095.5) * mm});
            skLineSegment(sketch, "E12.52.0.5", {"start": v(7264.4, 12.7) * mm, "end": v(7391.4, 12.7) * mm});
            skLineSegment(sketch, "E12.52.0.6", {"start": v(7391.4, 1041.4) * mm, "end": v(7264.4, 1041.4) * mm});
            skLineSegment(sketch, "E12.52.0.7", {"start": v(7391.4, 1066.8) * mm, "end": v(7264.4, 1066.8) * mm});
            skLineSegment(sketch, "E12.52.1.0", {"start": v(7264.4, 1041.4) * mm, "end": v(7264.4, 0) * mm});
            skLineSegment(sketch, "E12.52.1.1", {"start": v(7264.4, 1066.8) * mm, "end": v(7264.4, 2095.5) * mm});
            skLineSegment(sketch, "E12.52.1.2", {"start": v(7391.4, 12.7) * mm, "end": v(7391.4, 1041.4) * mm});
            skLineSegment(sketch, "E12.52.1.3", {"start": v(7391.4, 2095.5) * mm, "end": v(7391.4, 1066.8) * mm});
            skLineSegment(sketch, "E12.52.1.4", {"start": v(7264.4, 2095.5) * mm, "end": v(7391.4, 2095.5) * mm});
            skLineSegment(sketch, "E12.52.1.5", {"start": v(7264.4, 12.7) * mm, "end": v(7391.4, 12.7) * mm});
            skLineSegment(sketch, "E12.52.1.6", {"start": v(7391.4, 1041.4) * mm, "end": v(7264.4, 1041.4) * mm});
            skLineSegment(sketch, "E12.52.1.7", {"start": v(7391.4, 1066.8) * mm, "end": v(7264.4, 1066.8) * mm});
            skLineSegment(sketch, "E12.53.0.0", {"start": v(7404.1, 1041.4) * mm, "end": v(7404.1, 0) * mm});
            skLineSegment(sketch, "E12.53.0.1", {"start": v(7404.1, 1066.8) * mm, "end": v(7404.1, 2095.5) * mm});
            skLineSegment(sketch, "E12.53.0.2", {"start": v(7531.1, 12.7) * mm, "end": v(7531.1, 1041.4) * mm});
            skLineSegment(sketch, "E12.53.0.3", {"start": v(7531.1, 2095.5) * mm, "end": v(7531.1, 1066.8) * mm});
            skLineSegment(sketch, "E12.53.0.4", {"start": v(7404.1, 2095.5) * mm, "end": v(7531.1, 2095.5) * mm});
            skLineSegment(sketch, "E12.53.0.5", {"start": v(7404.1, 12.7) * mm, "end": v(7531.1, 12.7) * mm});
            skLineSegment(sketch, "E12.53.0.6", {"start": v(7531.1, 1041.4) * mm, "end": v(7404.1, 1041.4) * mm});
            skLineSegment(sketch, "E12.53.0.7", {"start": v(7531.1, 1066.8) * mm, "end": v(7404.1, 1066.8) * mm});
            skLineSegment(sketch, "E12.53.1.0", {"start": v(7404.1, 1041.4) * mm, "end": v(7404.1, 0) * mm});
            skLineSegment(sketch, "E12.53.1.1", {"start": v(7404.1, 1066.8) * mm, "end": v(7404.1, 2095.5) * mm});
            skLineSegment(sketch, "E12.53.1.2", {"start": v(7531.1, 12.7) * mm, "end": v(7531.1, 1041.4) * mm});
            skLineSegment(sketch, "E12.53.1.3", {"start": v(7531.1, 2095.5) * mm, "end": v(7531.1, 1066.8) * mm});
            skLineSegment(sketch, "E12.53.1.4", {"start": v(7404.1, 2095.5) * mm, "end": v(7531.1, 2095.5) * mm});
            skLineSegment(sketch, "E12.53.1.5", {"start": v(7404.1, 12.7) * mm, "end": v(7531.1, 12.7) * mm});
            skLineSegment(sketch, "E12.53.1.6", {"start": v(7531.1, 1041.4) * mm, "end": v(7404.1, 1041.4) * mm});
            skLineSegment(sketch, "E12.53.1.7", {"start": v(7531.1, 1066.8) * mm, "end": v(7404.1, 1066.8) * mm});
            skLineSegment(sketch, "E12.54.0.0", {"start": v(7543.8, 1041.4) * mm, "end": v(7543.8, 0) * mm});
            skLineSegment(sketch, "E12.54.0.1", {"start": v(7543.8, 1066.8) * mm, "end": v(7543.8, 2095.5) * mm});
            skLineSegment(sketch, "E12.54.0.2", {"start": v(7670.8, 12.7) * mm, "end": v(7670.8, 1041.4) * mm});
            skLineSegment(sketch, "E12.54.0.3", {"start": v(7670.8, 2095.5) * mm, "end": v(7670.8, 1066.8) * mm});
            skLineSegment(sketch, "E12.54.0.4", {"start": v(7543.8, 2095.5) * mm, "end": v(7670.8, 2095.5) * mm});
            skLineSegment(sketch, "E12.54.0.5", {"start": v(7543.8, 12.7) * mm, "end": v(7670.8, 12.7) * mm});
            skLineSegment(sketch, "E12.54.0.6", {"start": v(7670.8, 1041.4) * mm, "end": v(7543.8, 1041.4) * mm});
            skLineSegment(sketch, "E12.54.0.7", {"start": v(7670.8, 1066.8) * mm, "end": v(7543.8, 1066.8) * mm});
            skLineSegment(sketch, "E12.54.1.0", {"start": v(7543.8, 1041.4) * mm, "end": v(7543.8, 0) * mm});
            skLineSegment(sketch, "E12.54.1.1", {"start": v(7543.8, 1066.8) * mm, "end": v(7543.8, 2095.5) * mm});
            skLineSegment(sketch, "E12.54.1.2", {"start": v(7670.8, 12.7) * mm, "end": v(7670.8, 1041.4) * mm});
            skLineSegment(sketch, "E12.54.1.3", {"start": v(7670.8, 2095.5) * mm, "end": v(7670.8, 1066.8) * mm});
            skLineSegment(sketch, "E12.54.1.4", {"start": v(7543.8, 2095.5) * mm, "end": v(7670.8, 2095.5) * mm});
            skLineSegment(sketch, "E12.54.1.5", {"start": v(7543.8, 12.7) * mm, "end": v(7670.8, 12.7) * mm});
            skLineSegment(sketch, "E12.54.1.6", {"start": v(7670.8, 1041.4) * mm, "end": v(7543.8, 1041.4) * mm});
            skLineSegment(sketch, "E12.54.1.7", {"start": v(7670.8, 1066.8) * mm, "end": v(7543.8, 1066.8) * mm});
            skLineSegment(sketch, "E12.55.0.0", {"start": v(7683.5, 1041.4) * mm, "end": v(7683.5, 0) * mm});
            skLineSegment(sketch, "E12.55.0.1", {"start": v(7683.5, 1066.8) * mm, "end": v(7683.5, 2095.5) * mm});
            skLineSegment(sketch, "E12.55.0.2", {"start": v(7810.5, 12.7) * mm, "end": v(7810.5, 1041.4) * mm});
            skLineSegment(sketch, "E12.55.0.3", {"start": v(7810.5, 2095.5) * mm, "end": v(7810.5, 1066.8) * mm});
            skLineSegment(sketch, "E12.55.0.4", {"start": v(7683.5, 2095.5) * mm, "end": v(7810.5, 2095.5) * mm});
            skLineSegment(sketch, "E12.55.0.5", {"start": v(7683.5, 12.7) * mm, "end": v(7810.5, 12.7) * mm});
            skLineSegment(sketch, "E12.55.0.6", {"start": v(7810.5, 1041.4) * mm, "end": v(7683.5, 1041.4) * mm});
            skLineSegment(sketch, "E12.55.0.7", {"start": v(7810.5, 1066.8) * mm, "end": v(7683.5, 1066.8) * mm});
            skLineSegment(sketch, "E12.55.1.0", {"start": v(7683.5, 1041.4) * mm, "end": v(7683.5, 0) * mm});
            skLineSegment(sketch, "E12.55.1.1", {"start": v(7683.5, 1066.8) * mm, "end": v(7683.5, 2095.5) * mm});
            skLineSegment(sketch, "E12.55.1.2", {"start": v(7810.5, 12.7) * mm, "end": v(7810.5, 1041.4) * mm});
            skLineSegment(sketch, "E12.55.1.3", {"start": v(7810.5, 2095.5) * mm, "end": v(7810.5, 1066.8) * mm});
            skLineSegment(sketch, "E12.55.1.4", {"start": v(7683.5, 2095.5) * mm, "end": v(7810.5, 2095.5) * mm});
            skLineSegment(sketch, "E12.55.1.5", {"start": v(7683.5, 12.7) * mm, "end": v(7810.5, 12.7) * mm});
            skLineSegment(sketch, "E12.55.1.6", {"start": v(7810.5, 1041.4) * mm, "end": v(7683.5, 1041.4) * mm});
            skLineSegment(sketch, "E12.55.1.7", {"start": v(7810.5, 1066.8) * mm, "end": v(7683.5, 1066.8) * mm});
            skLineSegment(sketch, "E12.56.0.0", {"start": v(7823.2, 1041.4) * mm, "end": v(7823.2, 0) * mm});
            skLineSegment(sketch, "E12.56.0.1", {"start": v(7823.2, 1066.8) * mm, "end": v(7823.2, 2095.5) * mm});
            skLineSegment(sketch, "E12.56.0.2", {"start": v(7950.2, 12.7) * mm, "end": v(7950.2, 1041.4) * mm});
            skLineSegment(sketch, "E12.56.0.3", {"start": v(7950.2, 2095.5) * mm, "end": v(7950.2, 1066.8) * mm});
            skLineSegment(sketch, "E12.56.0.4", {"start": v(7823.2, 2095.5) * mm, "end": v(7950.2, 2095.5) * mm});
            skLineSegment(sketch, "E12.56.0.5", {"start": v(7823.2, 12.7) * mm, "end": v(7950.2, 12.7) * mm});
            skLineSegment(sketch, "E12.56.0.6", {"start": v(7950.2, 1041.4) * mm, "end": v(7823.2, 1041.4) * mm});
            skLineSegment(sketch, "E12.56.0.7", {"start": v(7950.2, 1066.8) * mm, "end": v(7823.2, 1066.8) * mm});
            skLineSegment(sketch, "E12.56.1.0", {"start": v(7823.2, 1041.4) * mm, "end": v(7823.2, 0) * mm});
            skLineSegment(sketch, "E12.56.1.1", {"start": v(7823.2, 1066.8) * mm, "end": v(7823.2, 2095.5) * mm});
            skLineSegment(sketch, "E12.56.1.2", {"start": v(7950.2, 12.7) * mm, "end": v(7950.2, 1041.4) * mm});
            skLineSegment(sketch, "E12.56.1.3", {"start": v(7950.2, 2095.5) * mm, "end": v(7950.2, 1066.8) * mm});
            skLineSegment(sketch, "E12.56.1.4", {"start": v(7823.2, 2095.5) * mm, "end": v(7950.2, 2095.5) * mm});
            skLineSegment(sketch, "E12.56.1.5", {"start": v(7823.2, 12.7) * mm, "end": v(7950.2, 12.7) * mm});
            skLineSegment(sketch, "E12.56.1.6", {"start": v(7950.2, 1041.4) * mm, "end": v(7823.2, 1041.4) * mm});
            skLineSegment(sketch, "E12.56.1.7", {"start": v(7950.2, 1066.8) * mm, "end": v(7823.2, 1066.8) * mm});
            skLineSegment(sketch, "E12.57.0.0", {"start": v(7962.9, 1041.4) * mm, "end": v(7962.9, 0) * mm});
            skLineSegment(sketch, "E12.57.0.1", {"start": v(7962.9, 1066.8) * mm, "end": v(7962.9, 2095.5) * mm});
            skLineSegment(sketch, "E12.57.0.2", {"start": v(8089.9, 12.7) * mm, "end": v(8089.9, 1041.4) * mm});
            skLineSegment(sketch, "E12.57.0.3", {"start": v(8089.9, 2095.5) * mm, "end": v(8089.9, 1066.8) * mm});
            skLineSegment(sketch, "E12.57.0.4", {"start": v(7962.9, 2095.5) * mm, "end": v(8089.9, 2095.5) * mm});
            skLineSegment(sketch, "E12.57.0.5", {"start": v(7962.9, 12.7) * mm, "end": v(8089.9, 12.7) * mm});
            skLineSegment(sketch, "E12.57.0.6", {"start": v(8089.9, 1041.4) * mm, "end": v(7962.9, 1041.4) * mm});
            skLineSegment(sketch, "E12.57.0.7", {"start": v(8089.9, 1066.8) * mm, "end": v(7962.9, 1066.8) * mm});
            skLineSegment(sketch, "E12.57.1.0", {"start": v(7962.9, 1041.4) * mm, "end": v(7962.9, 0) * mm});
            skLineSegment(sketch, "E12.57.1.1", {"start": v(7962.9, 1066.8) * mm, "end": v(7962.9, 2095.5) * mm});
            skLineSegment(sketch, "E12.57.1.2", {"start": v(8089.9, 12.7) * mm, "end": v(8089.9, 1041.4) * mm});
            skLineSegment(sketch, "E12.57.1.3", {"start": v(8089.9, 2095.5) * mm, "end": v(8089.9, 1066.8) * mm});
            skLineSegment(sketch, "E12.57.1.4", {"start": v(7962.9, 2095.5) * mm, "end": v(8089.9, 2095.5) * mm});
            skLineSegment(sketch, "E12.57.1.5", {"start": v(7962.9, 12.7) * mm, "end": v(8089.9, 12.7) * mm});
            skLineSegment(sketch, "E12.57.1.6", {"start": v(8089.9, 1041.4) * mm, "end": v(7962.9, 1041.4) * mm});
            skLineSegment(sketch, "E12.57.1.7", {"start": v(8089.9, 1066.8) * mm, "end": v(7962.9, 1066.8) * mm});
            skLineSegment(sketch, "E12.58.0.0", {"start": v(8102.6, 1041.4) * mm, "end": v(8102.6, 0) * mm});
            skLineSegment(sketch, "E12.58.0.1", {"start": v(8102.6, 1066.8) * mm, "end": v(8102.6, 2095.5) * mm});
            skLineSegment(sketch, "E12.58.0.2", {"start": v(8229.6, 12.7) * mm, "end": v(8229.6, 1041.4) * mm});
            skLineSegment(sketch, "E12.58.0.3", {"start": v(8229.6, 2095.5) * mm, "end": v(8229.6, 1066.8) * mm});
            skLineSegment(sketch, "E12.58.0.4", {"start": v(8102.6, 2095.5) * mm, "end": v(8229.6, 2095.5) * mm});
            skLineSegment(sketch, "E12.58.0.5", {"start": v(8102.6, 12.7) * mm, "end": v(8229.6, 12.7) * mm});
            skLineSegment(sketch, "E12.58.0.6", {"start": v(8229.6, 1041.4) * mm, "end": v(8102.6, 1041.4) * mm});
            skLineSegment(sketch, "E12.58.0.7", {"start": v(8229.6, 1066.8) * mm, "end": v(8102.6, 1066.8) * mm});
            skLineSegment(sketch, "E12.58.1.0", {"start": v(8102.6, 1041.4) * mm, "end": v(8102.6, 0) * mm});
            skLineSegment(sketch, "E12.58.1.1", {"start": v(8102.6, 1066.8) * mm, "end": v(8102.6, 2095.5) * mm});
            skLineSegment(sketch, "E12.58.1.2", {"start": v(8229.6, 12.7) * mm, "end": v(8229.6, 1041.4) * mm});
            skLineSegment(sketch, "E12.58.1.3", {"start": v(8229.6, 2095.5) * mm, "end": v(8229.6, 1066.8) * mm});
            skLineSegment(sketch, "E12.58.1.4", {"start": v(8102.6, 2095.5) * mm, "end": v(8229.6, 2095.5) * mm});
            skLineSegment(sketch, "E12.58.1.5", {"start": v(8102.6, 12.7) * mm, "end": v(8229.6, 12.7) * mm});
            skLineSegment(sketch, "E12.58.1.6", {"start": v(8229.6, 1041.4) * mm, "end": v(8102.6, 1041.4) * mm});
            skLineSegment(sketch, "E12.58.1.7", {"start": v(8229.6, 1066.8) * mm, "end": v(8102.6, 1066.8) * mm});
            skLineSegment(sketch, "E12.59.0.0", {"start": v(8242.3, 1041.4) * mm, "end": v(8242.3, 0) * mm});
            skLineSegment(sketch, "E12.59.0.1", {"start": v(8242.3, 1066.8) * mm, "end": v(8242.3, 2095.5) * mm});
            skLineSegment(sketch, "E12.59.0.2", {"start": v(8369.3, 12.7) * mm, "end": v(8369.3, 1041.4) * mm});
            skLineSegment(sketch, "E12.59.0.3", {"start": v(8369.3, 2095.5) * mm, "end": v(8369.3, 1066.8) * mm});
            skLineSegment(sketch, "E12.59.0.4", {"start": v(8242.3, 2095.5) * mm, "end": v(8369.3, 2095.5) * mm});
            skLineSegment(sketch, "E12.59.0.5", {"start": v(8242.3, 12.7) * mm, "end": v(8369.3, 12.7) * mm});
            skLineSegment(sketch, "E12.59.0.6", {"start": v(8369.3, 1041.4) * mm, "end": v(8242.3, 1041.4) * mm});
            skLineSegment(sketch, "E12.59.0.7", {"start": v(8369.3, 1066.8) * mm, "end": v(8242.3, 1066.8) * mm});
            skLineSegment(sketch, "E12.59.1.0", {"start": v(8242.3, 1041.4) * mm, "end": v(8242.3, 0) * mm});
            skLineSegment(sketch, "E12.59.1.1", {"start": v(8242.3, 1066.8) * mm, "end": v(8242.3, 2095.5) * mm});
            skLineSegment(sketch, "E12.59.1.2", {"start": v(8369.3, 12.7) * mm, "end": v(8369.3, 1041.4) * mm});
            skLineSegment(sketch, "E12.59.1.3", {"start": v(8369.3, 2095.5) * mm, "end": v(8369.3, 1066.8) * mm});
            skLineSegment(sketch, "E12.59.1.4", {"start": v(8242.3, 2095.5) * mm, "end": v(8369.3, 2095.5) * mm});
            skLineSegment(sketch, "E12.59.1.5", {"start": v(8242.3, 12.7) * mm, "end": v(8369.3, 12.7) * mm});
            skLineSegment(sketch, "E12.59.1.6", {"start": v(8369.3, 1041.4) * mm, "end": v(8242.3, 1041.4) * mm});
            skLineSegment(sketch, "E12.59.1.7", {"start": v(8369.3, 1066.8) * mm, "end": v(8242.3, 1066.8) * mm});
            skLineSegment(sketch, "E12.60.0.0", {"start": v(8382, 1041.4) * mm, "end": v(8382, 0) * mm});
            skLineSegment(sketch, "E12.60.0.1", {"start": v(8382, 1066.8) * mm, "end": v(8382, 2095.5) * mm});
            skLineSegment(sketch, "E12.60.0.2", {"start": v(8509, 12.7) * mm, "end": v(8509, 1041.4) * mm});
            skLineSegment(sketch, "E12.60.0.3", {"start": v(8509, 2095.5) * mm, "end": v(8509, 1066.8) * mm});
            skLineSegment(sketch, "E12.60.0.4", {"start": v(8382, 2095.5) * mm, "end": v(8509, 2095.5) * mm});
            skLineSegment(sketch, "E12.60.0.5", {"start": v(8382, 12.7) * mm, "end": v(8509, 12.7) * mm});
            skLineSegment(sketch, "E12.60.0.6", {"start": v(8509, 1041.4) * mm, "end": v(8382, 1041.4) * mm});
            skLineSegment(sketch, "E12.60.0.7", {"start": v(8509, 1066.8) * mm, "end": v(8382, 1066.8) * mm});
            skLineSegment(sketch, "E12.60.1.0", {"start": v(8382, 1041.4) * mm, "end": v(8382, 0) * mm});
            skLineSegment(sketch, "E12.60.1.1", {"start": v(8382, 1066.8) * mm, "end": v(8382, 2095.5) * mm});
            skLineSegment(sketch, "E12.60.1.2", {"start": v(8509, 12.7) * mm, "end": v(8509, 1041.4) * mm});
            skLineSegment(sketch, "E12.60.1.3", {"start": v(8509, 2095.5) * mm, "end": v(8509, 1066.8) * mm});
            skLineSegment(sketch, "E12.60.1.4", {"start": v(8382, 2095.5) * mm, "end": v(8509, 2095.5) * mm});
            skLineSegment(sketch, "E12.60.1.5", {"start": v(8382, 12.7) * mm, "end": v(8509, 12.7) * mm});
            skLineSegment(sketch, "E12.60.1.6", {"start": v(8509, 1041.4) * mm, "end": v(8382, 1041.4) * mm});
            skLineSegment(sketch, "E12.60.1.7", {"start": v(8509, 1066.8) * mm, "end": v(8382, 1066.8) * mm});
            skLineSegment(sketch, "E12.61.0.0", {"start": v(8521.7, 1041.4) * mm, "end": v(8521.7, 0) * mm});
            skLineSegment(sketch, "E12.61.0.1", {"start": v(8521.7, 1066.8) * mm, "end": v(8521.7, 2095.5) * mm});
            skLineSegment(sketch, "E12.61.0.2", {"start": v(8648.7, 12.7) * mm, "end": v(8648.7, 1041.4) * mm});
            skLineSegment(sketch, "E12.61.0.3", {"start": v(8648.7, 2095.5) * mm, "end": v(8648.7, 1066.8) * mm});
            skLineSegment(sketch, "E12.61.0.4", {"start": v(8521.7, 2095.5) * mm, "end": v(8648.7, 2095.5) * mm});
            skLineSegment(sketch, "E12.61.0.5", {"start": v(8521.7, 12.7) * mm, "end": v(8648.7, 12.7) * mm});
            skLineSegment(sketch, "E12.61.0.6", {"start": v(8648.7, 1041.4) * mm, "end": v(8521.7, 1041.4) * mm});
            skLineSegment(sketch, "E12.61.0.7", {"start": v(8648.7, 1066.8) * mm, "end": v(8521.7, 1066.8) * mm});
            skLineSegment(sketch, "E12.61.1.0", {"start": v(8521.7, 1041.4) * mm, "end": v(8521.7, 0) * mm});
            skLineSegment(sketch, "E12.61.1.1", {"start": v(8521.7, 1066.8) * mm, "end": v(8521.7, 2095.5) * mm});
            skLineSegment(sketch, "E12.61.1.2", {"start": v(8648.7, 12.7) * mm, "end": v(8648.7, 1041.4) * mm});
            skLineSegment(sketch, "E12.61.1.3", {"start": v(8648.7, 2095.5) * mm, "end": v(8648.7, 1066.8) * mm});
            skLineSegment(sketch, "E12.61.1.4", {"start": v(8521.7, 2095.5) * mm, "end": v(8648.7, 2095.5) * mm});
            skLineSegment(sketch, "E12.61.1.5", {"start": v(8521.7, 12.7) * mm, "end": v(8648.7, 12.7) * mm});
            skLineSegment(sketch, "E12.61.1.6", {"start": v(8648.7, 1041.4) * mm, "end": v(8521.7, 1041.4) * mm});
            skLineSegment(sketch, "E12.61.1.7", {"start": v(8648.7, 1066.8) * mm, "end": v(8521.7, 1066.8) * mm});
            skLineSegment(sketch, "E12.62.0.0", {"start": v(8661.4, 1041.4) * mm, "end": v(8661.4, 0) * mm});
            skLineSegment(sketch, "E12.62.0.1", {"start": v(8661.4, 1066.8) * mm, "end": v(8661.4, 2095.5) * mm});
            skLineSegment(sketch, "E12.62.0.2", {"start": v(8788.4, 12.7) * mm, "end": v(8788.4, 1041.4) * mm});
            skLineSegment(sketch, "E12.62.0.3", {"start": v(8788.4, 2095.5) * mm, "end": v(8788.4, 1066.8) * mm});
            skLineSegment(sketch, "E12.62.0.4", {"start": v(8661.4, 2095.5) * mm, "end": v(8788.4, 2095.5) * mm});
            skLineSegment(sketch, "E12.62.0.5", {"start": v(8661.4, 12.7) * mm, "end": v(8788.4, 12.7) * mm});
            skLineSegment(sketch, "E12.62.0.6", {"start": v(8788.4, 1041.4) * mm, "end": v(8661.4, 1041.4) * mm});
            skLineSegment(sketch, "E12.62.0.7", {"start": v(8788.4, 1066.8) * mm, "end": v(8661.4, 1066.8) * mm});
            skLineSegment(sketch, "E12.62.1.0", {"start": v(8661.4, 1041.4) * mm, "end": v(8661.4, 0) * mm});
            skLineSegment(sketch, "E12.62.1.1", {"start": v(8661.4, 1066.8) * mm, "end": v(8661.4, 2095.5) * mm});
            skLineSegment(sketch, "E12.62.1.2", {"start": v(8788.4, 12.7) * mm, "end": v(8788.4, 1041.4) * mm});
            skLineSegment(sketch, "E12.62.1.3", {"start": v(8788.4, 2095.5) * mm, "end": v(8788.4, 1066.8) * mm});
            skLineSegment(sketch, "E12.62.1.4", {"start": v(8661.4, 2095.5) * mm, "end": v(8788.4, 2095.5) * mm});
            skLineSegment(sketch, "E12.62.1.5", {"start": v(8661.4, 12.7) * mm, "end": v(8788.4, 12.7) * mm});
            skLineSegment(sketch, "E12.62.1.6", {"start": v(8788.4, 1041.4) * mm, "end": v(8661.4, 1041.4) * mm});
            skLineSegment(sketch, "E12.62.1.7", {"start": v(8788.4, 1066.8) * mm, "end": v(8661.4, 1066.8) * mm});
            skLineSegment(sketch, "E12.63.0.0", {"start": v(8801.1, 1041.4) * mm, "end": v(8801.1, 0) * mm});
            skLineSegment(sketch, "E12.63.0.1", {"start": v(8801.1, 1066.8) * mm, "end": v(8801.1, 2095.5) * mm});
            skLineSegment(sketch, "E12.63.0.2", {"start": v(8928.1, 12.7) * mm, "end": v(8928.1, 1041.4) * mm});
            skLineSegment(sketch, "E12.63.0.3", {"start": v(8928.1, 2095.5) * mm, "end": v(8928.1, 1066.8) * mm});
            skLineSegment(sketch, "E12.63.0.4", {"start": v(8801.1, 2095.5) * mm, "end": v(8928.1, 2095.5) * mm});
            skLineSegment(sketch, "E12.63.0.5", {"start": v(8801.1, 12.7) * mm, "end": v(8928.1, 12.7) * mm});
            skLineSegment(sketch, "E12.63.0.6", {"start": v(8928.1, 1041.4) * mm, "end": v(8801.1, 1041.4) * mm});
            skLineSegment(sketch, "E12.63.0.7", {"start": v(8928.1, 1066.8) * mm, "end": v(8801.1, 1066.8) * mm});
            skLineSegment(sketch, "E12.63.1.0", {"start": v(8801.1, 1041.4) * mm, "end": v(8801.1, 0) * mm});
            skLineSegment(sketch, "E12.63.1.1", {"start": v(8801.1, 1066.8) * mm, "end": v(8801.1, 2095.5) * mm});
            skLineSegment(sketch, "E12.63.1.2", {"start": v(8928.1, 12.7) * mm, "end": v(8928.1, 1041.4) * mm});
            skLineSegment(sketch, "E12.63.1.3", {"start": v(8928.1, 2095.5) * mm, "end": v(8928.1, 1066.8) * mm});
            skLineSegment(sketch, "E12.63.1.4", {"start": v(8801.1, 2095.5) * mm, "end": v(8928.1, 2095.5) * mm});
            skLineSegment(sketch, "E12.63.1.5", {"start": v(8801.1, 12.7) * mm, "end": v(8928.1, 12.7) * mm});
            skLineSegment(sketch, "E12.63.1.6", {"start": v(8928.1, 1041.4) * mm, "end": v(8801.1, 1041.4) * mm});
            skLineSegment(sketch, "E12.63.1.7", {"start": v(8928.1, 1066.8) * mm, "end": v(8801.1, 1066.8) * mm});
            skLineSegment(sketch, "E12.64.0.0", {"start": v(8940.8, 1041.4) * mm, "end": v(8940.8, 0) * mm});
            skLineSegment(sketch, "E12.64.0.1", {"start": v(8940.8, 1066.8) * mm, "end": v(8940.8, 2095.5) * mm});
            skLineSegment(sketch, "E12.64.0.2", {"start": v(9067.8, 12.7) * mm, "end": v(9067.8, 1041.4) * mm});
            skLineSegment(sketch, "E12.64.0.3", {"start": v(9067.8, 2095.5) * mm, "end": v(9067.8, 1066.8) * mm});
            skLineSegment(sketch, "E12.64.0.4", {"start": v(8940.8, 2095.5) * mm, "end": v(9067.8, 2095.5) * mm});
            skLineSegment(sketch, "E12.64.0.5", {"start": v(8940.8, 12.7) * mm, "end": v(9067.8, 12.7) * mm});
            skLineSegment(sketch, "E12.64.0.6", {"start": v(9067.8, 1041.4) * mm, "end": v(8940.8, 1041.4) * mm});
            skLineSegment(sketch, "E12.64.0.7", {"start": v(9067.8, 1066.8) * mm, "end": v(8940.8, 1066.8) * mm});
            skLineSegment(sketch, "E12.64.1.0", {"start": v(8940.8, 1041.4) * mm, "end": v(8940.8, 0) * mm});
            skLineSegment(sketch, "E12.64.1.1", {"start": v(8940.8, 1066.8) * mm, "end": v(8940.8, 2095.5) * mm});
            skLineSegment(sketch, "E12.64.1.2", {"start": v(9067.8, 12.7) * mm, "end": v(9067.8, 1041.4) * mm});
            skLineSegment(sketch, "E12.64.1.3", {"start": v(9067.8, 2095.5) * mm, "end": v(9067.8, 1066.8) * mm});
            skLineSegment(sketch, "E12.64.1.4", {"start": v(8940.8, 2095.5) * mm, "end": v(9067.8, 2095.5) * mm});
            skLineSegment(sketch, "E12.64.1.5", {"start": v(8940.8, 12.7) * mm, "end": v(9067.8, 12.7) * mm});
            skLineSegment(sketch, "E12.64.1.6", {"start": v(9067.8, 1041.4) * mm, "end": v(8940.8, 1041.4) * mm});
            skLineSegment(sketch, "E12.64.1.7", {"start": v(9067.8, 1066.8) * mm, "end": v(8940.8, 1066.8) * mm});
            skLineSegment(sketch, "E12.65.0.0", {"start": v(9080.5, 1041.4) * mm, "end": v(9080.5, 0) * mm});
            skLineSegment(sketch, "E12.65.0.1", {"start": v(9080.5, 1066.8) * mm, "end": v(9080.5, 2095.5) * mm});
            skLineSegment(sketch, "E12.65.0.2", {"start": v(9207.5, 12.7) * mm, "end": v(9207.5, 1041.4) * mm});
            skLineSegment(sketch, "E12.65.0.3", {"start": v(9207.5, 2095.5) * mm, "end": v(9207.5, 1066.8) * mm});
            skLineSegment(sketch, "E12.65.0.4", {"start": v(9080.5, 2095.5) * mm, "end": v(9207.5, 2095.5) * mm});
            skLineSegment(sketch, "E12.65.0.5", {"start": v(9080.5, 12.7) * mm, "end": v(9207.5, 12.7) * mm});
            skLineSegment(sketch, "E12.65.0.6", {"start": v(9207.5, 1041.4) * mm, "end": v(9080.5, 1041.4) * mm});
            skLineSegment(sketch, "E12.65.0.7", {"start": v(9207.5, 1066.8) * mm, "end": v(9080.5, 1066.8) * mm});
            skLineSegment(sketch, "E12.65.1.0", {"start": v(9080.5, 1041.4) * mm, "end": v(9080.5, 0) * mm});
            skLineSegment(sketch, "E12.65.1.1", {"start": v(9080.5, 1066.8) * mm, "end": v(9080.5, 2095.5) * mm});
            skLineSegment(sketch, "E12.65.1.2", {"start": v(9207.5, 12.7) * mm, "end": v(9207.5, 1041.4) * mm});
            skLineSegment(sketch, "E12.65.1.3", {"start": v(9207.5, 2095.5) * mm, "end": v(9207.5, 1066.8) * mm});
            skLineSegment(sketch, "E12.65.1.4", {"start": v(9080.5, 2095.5) * mm, "end": v(9207.5, 2095.5) * mm});
            skLineSegment(sketch, "E12.65.1.5", {"start": v(9080.5, 12.7) * mm, "end": v(9207.5, 12.7) * mm});
            skLineSegment(sketch, "E12.65.1.6", {"start": v(9207.5, 1041.4) * mm, "end": v(9080.5, 1041.4) * mm});
            skLineSegment(sketch, "E12.65.1.7", {"start": v(9207.5, 1066.8) * mm, "end": v(9080.5, 1066.8) * mm});
            skLineSegment(sketch, "E12.66.0.0", {"start": v(9220.2, 1041.4) * mm, "end": v(9220.2, 0) * mm});
            skLineSegment(sketch, "E12.66.0.1", {"start": v(9220.2, 1066.8) * mm, "end": v(9220.2, 2095.5) * mm});
            skLineSegment(sketch, "E12.66.0.2", {"start": v(9347.2, 12.7) * mm, "end": v(9347.2, 1041.4) * mm});
            skLineSegment(sketch, "E12.66.0.3", {"start": v(9347.2, 2095.5) * mm, "end": v(9347.2, 1066.8) * mm});
            skLineSegment(sketch, "E12.66.0.4", {"start": v(9220.2, 2095.5) * mm, "end": v(9347.2, 2095.5) * mm});
            skLineSegment(sketch, "E12.66.0.5", {"start": v(9220.2, 12.7) * mm, "end": v(9347.2, 12.7) * mm});
            skLineSegment(sketch, "E12.66.0.6", {"start": v(9347.2, 1041.4) * mm, "end": v(9220.2, 1041.4) * mm});
            skLineSegment(sketch, "E12.66.0.7", {"start": v(9347.2, 1066.8) * mm, "end": v(9220.2, 1066.8) * mm});
            skLineSegment(sketch, "E12.66.1.0", {"start": v(9220.2, 1041.4) * mm, "end": v(9220.2, 0) * mm});
            skLineSegment(sketch, "E12.66.1.1", {"start": v(9220.2, 1066.8) * mm, "end": v(9220.2, 2095.5) * mm});
            skLineSegment(sketch, "E12.66.1.2", {"start": v(9347.2, 12.7) * mm, "end": v(9347.2, 1041.4) * mm});
            skLineSegment(sketch, "E12.66.1.3", {"start": v(9347.2, 2095.5) * mm, "end": v(9347.2, 1066.8) * mm});
            skLineSegment(sketch, "E12.66.1.4", {"start": v(9220.2, 2095.5) * mm, "end": v(9347.2, 2095.5) * mm});
            skLineSegment(sketch, "E12.66.1.5", {"start": v(9220.2, 12.7) * mm, "end": v(9347.2, 12.7) * mm});
            skLineSegment(sketch, "E12.66.1.6", {"start": v(9347.2, 1041.4) * mm, "end": v(9220.2, 1041.4) * mm});
            skLineSegment(sketch, "E12.66.1.7", {"start": v(9347.2, 1066.8) * mm, "end": v(9220.2, 1066.8) * mm});
            skLineSegment(sketch, "E12.67.0.0", {"start": v(9359.9, 1041.4) * mm, "end": v(9359.9, 0) * mm});
            skLineSegment(sketch, "E12.67.0.1", {"start": v(9359.9, 1066.8) * mm, "end": v(9359.9, 2095.5) * mm});
            skLineSegment(sketch, "E12.67.0.2", {"start": v(9486.9, 12.7) * mm, "end": v(9486.9, 1041.4) * mm});
            skLineSegment(sketch, "E12.67.0.3", {"start": v(9486.9, 2095.5) * mm, "end": v(9486.9, 1066.8) * mm});
            skLineSegment(sketch, "E12.67.0.4", {"start": v(9359.9, 2095.5) * mm, "end": v(9486.9, 2095.5) * mm});
            skLineSegment(sketch, "E12.67.0.5", {"start": v(9359.9, 12.7) * mm, "end": v(9486.9, 12.7) * mm});
            skLineSegment(sketch, "E12.67.0.6", {"start": v(9486.9, 1041.4) * mm, "end": v(9359.9, 1041.4) * mm});
            skLineSegment(sketch, "E12.67.0.7", {"start": v(9486.9, 1066.8) * mm, "end": v(9359.9, 1066.8) * mm});
            skLineSegment(sketch, "E12.67.1.0", {"start": v(9359.9, 1041.4) * mm, "end": v(9359.9, 0) * mm});
            skLineSegment(sketch, "E12.67.1.1", {"start": v(9359.9, 1066.8) * mm, "end": v(9359.9, 2095.5) * mm});
            skLineSegment(sketch, "E12.67.1.2", {"start": v(9486.9, 12.7) * mm, "end": v(9486.9, 1041.4) * mm});
            skLineSegment(sketch, "E12.67.1.3", {"start": v(9486.9, 2095.5) * mm, "end": v(9486.9, 1066.8) * mm});
            skLineSegment(sketch, "E12.67.1.4", {"start": v(9359.9, 2095.5) * mm, "end": v(9486.9, 2095.5) * mm});
            skLineSegment(sketch, "E12.67.1.5", {"start": v(9359.9, 12.7) * mm, "end": v(9486.9, 12.7) * mm});
            skLineSegment(sketch, "E12.67.1.6", {"start": v(9486.9, 1041.4) * mm, "end": v(9359.9, 1041.4) * mm});
            skLineSegment(sketch, "E12.67.1.7", {"start": v(9486.9, 1066.8) * mm, "end": v(9359.9, 1066.8) * mm});
            skLineSegment(sketch, "E12.68.0.0", {"start": v(9499.6, 1041.4) * mm, "end": v(9499.6, 0) * mm});
            skLineSegment(sketch, "E12.68.0.1", {"start": v(9499.6, 1066.8) * mm, "end": v(9499.6, 2095.5) * mm});
            skLineSegment(sketch, "E12.68.0.2", {"start": v(9626.6, 12.7) * mm, "end": v(9626.6, 1041.4) * mm});
            skLineSegment(sketch, "E12.68.0.3", {"start": v(9626.6, 2095.5) * mm, "end": v(9626.6, 1066.8) * mm});
            skLineSegment(sketch, "E12.68.0.4", {"start": v(9499.6, 2095.5) * mm, "end": v(9626.6, 2095.5) * mm});
            skLineSegment(sketch, "E12.68.0.5", {"start": v(9499.6, 12.7) * mm, "end": v(9626.6, 12.7) * mm});
            skLineSegment(sketch, "E12.68.0.6", {"start": v(9626.6, 1041.4) * mm, "end": v(9499.6, 1041.4) * mm});
            skLineSegment(sketch, "E12.68.0.7", {"start": v(9626.6, 1066.8) * mm, "end": v(9499.6, 1066.8) * mm});
            skLineSegment(sketch, "E12.68.1.0", {"start": v(9499.6, 1041.4) * mm, "end": v(9499.6, 0) * mm});
            skLineSegment(sketch, "E12.68.1.1", {"start": v(9499.6, 1066.8) * mm, "end": v(9499.6, 2095.5) * mm});
            skLineSegment(sketch, "E12.68.1.2", {"start": v(9626.6, 12.7) * mm, "end": v(9626.6, 1041.4) * mm});
            skLineSegment(sketch, "E12.68.1.3", {"start": v(9626.6, 2095.5) * mm, "end": v(9626.6, 1066.8) * mm});
            skLineSegment(sketch, "E12.68.1.4", {"start": v(9499.6, 2095.5) * mm, "end": v(9626.6, 2095.5) * mm});
            skLineSegment(sketch, "E12.68.1.5", {"start": v(9499.6, 12.7) * mm, "end": v(9626.6, 12.7) * mm});
            skLineSegment(sketch, "E12.68.1.6", {"start": v(9626.6, 1041.4) * mm, "end": v(9499.6, 1041.4) * mm});
            skLineSegment(sketch, "E12.68.1.7", {"start": v(9626.6, 1066.8) * mm, "end": v(9499.6, 1066.8) * mm});
            skLineSegment(sketch, "E12.69.0.0", {"start": v(9639.3, 1041.4) * mm, "end": v(9639.3, 0) * mm});
            skLineSegment(sketch, "E12.69.0.1", {"start": v(9639.3, 1066.8) * mm, "end": v(9639.3, 2095.5) * mm});
            skLineSegment(sketch, "E12.69.0.2", {"start": v(9766.3, 12.7) * mm, "end": v(9766.3, 1041.4) * mm});
            skLineSegment(sketch, "E12.69.0.3", {"start": v(9766.3, 2095.5) * mm, "end": v(9766.3, 1066.8) * mm});
            skLineSegment(sketch, "E12.69.0.4", {"start": v(9639.3, 2095.5) * mm, "end": v(9766.3, 2095.5) * mm});
            skLineSegment(sketch, "E12.69.0.5", {"start": v(9639.3, 12.7) * mm, "end": v(9766.3, 12.7) * mm});
            skLineSegment(sketch, "E12.69.0.6", {"start": v(9766.3, 1041.4) * mm, "end": v(9639.3, 1041.4) * mm});
            skLineSegment(sketch, "E12.69.0.7", {"start": v(9766.3, 1066.8) * mm, "end": v(9639.3, 1066.8) * mm});
            skLineSegment(sketch, "E12.69.1.0", {"start": v(9639.3, 1041.4) * mm, "end": v(9639.3, 0) * mm});
            skLineSegment(sketch, "E12.69.1.1", {"start": v(9639.3, 1066.8) * mm, "end": v(9639.3, 2095.5) * mm});
            skLineSegment(sketch, "E12.69.1.2", {"start": v(9766.3, 12.7) * mm, "end": v(9766.3, 1041.4) * mm});
            skLineSegment(sketch, "E12.69.1.3", {"start": v(9766.3, 2095.5) * mm, "end": v(9766.3, 1066.8) * mm});
            skLineSegment(sketch, "E12.69.1.4", {"start": v(9639.3, 2095.5) * mm, "end": v(9766.3, 2095.5) * mm});
            skLineSegment(sketch, "E12.69.1.5", {"start": v(9639.3, 12.7) * mm, "end": v(9766.3, 12.7) * mm});
            skLineSegment(sketch, "E12.69.1.6", {"start": v(9766.3, 1041.4) * mm, "end": v(9639.3, 1041.4) * mm});
            skLineSegment(sketch, "E12.69.1.7", {"start": v(9766.3, 1066.8) * mm, "end": v(9639.3, 1066.8) * mm});
            skLineSegment(sketch, "E12.70.0.0", {"start": v(9779, 1041.4) * mm, "end": v(9779, 0) * mm});
            skLineSegment(sketch, "E12.70.0.1", {"start": v(9779, 1066.8) * mm, "end": v(9779, 2095.5) * mm});
            skLineSegment(sketch, "E12.70.0.2", {"start": v(9906, 12.7) * mm, "end": v(9906, 1041.4) * mm});
            skLineSegment(sketch, "E12.70.0.3", {"start": v(9906, 2095.5) * mm, "end": v(9906, 1066.8) * mm});
            skLineSegment(sketch, "E12.70.0.4", {"start": v(9779, 2095.5) * mm, "end": v(9906, 2095.5) * mm});
            skLineSegment(sketch, "E12.70.0.5", {"start": v(9779, 12.7) * mm, "end": v(9906, 12.7) * mm});
            skLineSegment(sketch, "E12.70.0.6", {"start": v(9906, 1041.4) * mm, "end": v(9779, 1041.4) * mm});
            skLineSegment(sketch, "E12.70.0.7", {"start": v(9906, 1066.8) * mm, "end": v(9779, 1066.8) * mm});
            skLineSegment(sketch, "E12.70.1.0", {"start": v(9779, 1041.4) * mm, "end": v(9779, 0) * mm});
            skLineSegment(sketch, "E12.70.1.1", {"start": v(9779, 1066.8) * mm, "end": v(9779, 2095.5) * mm});
            skLineSegment(sketch, "E12.70.1.2", {"start": v(9906, 12.7) * mm, "end": v(9906, 1041.4) * mm});
            skLineSegment(sketch, "E12.70.1.3", {"start": v(9906, 2095.5) * mm, "end": v(9906, 1066.8) * mm});
            skLineSegment(sketch, "E12.70.1.4", {"start": v(9779, 2095.5) * mm, "end": v(9906, 2095.5) * mm});
            skLineSegment(sketch, "E12.70.1.5", {"start": v(9779, 12.7) * mm, "end": v(9906, 12.7) * mm});
            skLineSegment(sketch, "E12.70.1.6", {"start": v(9906, 1041.4) * mm, "end": v(9779, 1041.4) * mm});
            skLineSegment(sketch, "E12.70.1.7", {"start": v(9906, 1066.8) * mm, "end": v(9779, 1066.8) * mm});
            skLineSegment(sketch, "E12.71.0.0", {"start": v(9918.7, 1041.4) * mm, "end": v(9918.7, 0) * mm});
            skLineSegment(sketch, "E12.71.0.1", {"start": v(9918.7, 1066.8) * mm, "end": v(9918.7, 2095.5) * mm});
            skLineSegment(sketch, "E12.71.0.2", {"start": v(10045.7, 12.7) * mm, "end": v(10045.7, 1041.4) * mm});
            skLineSegment(sketch, "E12.71.0.3", {"start": v(10045.7, 2095.5) * mm, "end": v(10045.7, 1066.8) * mm});
            skLineSegment(sketch, "E12.71.0.4", {"start": v(9918.7, 2095.5) * mm, "end": v(10045.7, 2095.5) * mm});
            skLineSegment(sketch, "E12.71.0.5", {"start": v(9918.7, 12.7) * mm, "end": v(10045.7, 12.7) * mm});
            skLineSegment(sketch, "E12.71.0.6", {"start": v(10045.7, 1041.4) * mm, "end": v(9918.7, 1041.4) * mm});
            skLineSegment(sketch, "E12.71.0.7", {"start": v(10045.7, 1066.8) * mm, "end": v(9918.7, 1066.8) * mm});
            skLineSegment(sketch, "E12.71.1.0", {"start": v(9918.7, 1041.4) * mm, "end": v(9918.7, 0) * mm});
            skLineSegment(sketch, "E12.71.1.1", {"start": v(9918.7, 1066.8) * mm, "end": v(9918.7, 2095.5) * mm});
            skLineSegment(sketch, "E12.71.1.2", {"start": v(10045.7, 12.7) * mm, "end": v(10045.7, 1041.4) * mm});
            skLineSegment(sketch, "E12.71.1.3", {"start": v(10045.7, 2095.5) * mm, "end": v(10045.7, 1066.8) * mm});
            skLineSegment(sketch, "E12.71.1.4", {"start": v(9918.7, 2095.5) * mm, "end": v(10045.7, 2095.5) * mm});
            skLineSegment(sketch, "E12.71.1.5", {"start": v(9918.7, 12.7) * mm, "end": v(10045.7, 12.7) * mm});
            skLineSegment(sketch, "E12.71.1.6", {"start": v(10045.7, 1041.4) * mm, "end": v(9918.7, 1041.4) * mm});
            skLineSegment(sketch, "E12.71.1.7", {"start": v(10045.7, 1066.8) * mm, "end": v(9918.7, 1066.8) * mm});
            skLineSegment(sketch, "E12.72.0.0", {"start": v(10058.4, 1041.4) * mm, "end": v(10058.4, 0) * mm});
            skLineSegment(sketch, "E12.72.0.1", {"start": v(10058.4, 1066.8) * mm, "end": v(10058.4, 2095.5) * mm});
            skLineSegment(sketch, "E12.72.0.2", {"start": v(10185.4, 12.7) * mm, "end": v(10185.4, 1041.4) * mm});
            skLineSegment(sketch, "E12.72.0.3", {"start": v(10185.4, 2095.5) * mm, "end": v(10185.4, 1066.8) * mm});
            skLineSegment(sketch, "E12.72.0.4", {"start": v(10058.4, 2095.5) * mm, "end": v(10185.4, 2095.5) * mm});
            skLineSegment(sketch, "E12.72.0.5", {"start": v(10058.4, 12.7) * mm, "end": v(10185.4, 12.7) * mm});
            skLineSegment(sketch, "E12.72.0.6", {"start": v(10185.4, 1041.4) * mm, "end": v(10058.4, 1041.4) * mm});
            skLineSegment(sketch, "E12.72.0.7", {"start": v(10185.4, 1066.8) * mm, "end": v(10058.4, 1066.8) * mm});
            skLineSegment(sketch, "E12.72.1.0", {"start": v(10058.4, 1041.4) * mm, "end": v(10058.4, 0) * mm});
            skLineSegment(sketch, "E12.72.1.1", {"start": v(10058.4, 1066.8) * mm, "end": v(10058.4, 2095.5) * mm});
            skLineSegment(sketch, "E12.72.1.2", {"start": v(10185.4, 12.7) * mm, "end": v(10185.4, 1041.4) * mm});
            skLineSegment(sketch, "E12.72.1.3", {"start": v(10185.4, 2095.5) * mm, "end": v(10185.4, 1066.8) * mm});
            skLineSegment(sketch, "E12.72.1.4", {"start": v(10058.4, 2095.5) * mm, "end": v(10185.4, 2095.5) * mm});
            skLineSegment(sketch, "E12.72.1.5", {"start": v(10058.4, 12.7) * mm, "end": v(10185.4, 12.7) * mm});
            skLineSegment(sketch, "E12.72.1.6", {"start": v(10185.4, 1041.4) * mm, "end": v(10058.4, 1041.4) * mm});
            skLineSegment(sketch, "E12.72.1.7", {"start": v(10185.4, 1066.8) * mm, "end": v(10058.4, 1066.8) * mm});
            skLineSegment(sketch, "E12.73.0.0", {"start": v(10198.1, 1041.4) * mm, "end": v(10198.1, 0) * mm});
            skLineSegment(sketch, "E12.73.0.1", {"start": v(10198.1, 1066.8) * mm, "end": v(10198.1, 2095.5) * mm});
            skLineSegment(sketch, "E12.73.0.2", {"start": v(10325.1, 12.7) * mm, "end": v(10325.1, 1041.4) * mm});
            skLineSegment(sketch, "E12.73.0.3", {"start": v(10325.1, 2095.5) * mm, "end": v(10325.1, 1066.8) * mm});
            skLineSegment(sketch, "E12.73.0.4", {"start": v(10198.1, 2095.5) * mm, "end": v(10325.1, 2095.5) * mm});
            skLineSegment(sketch, "E12.73.0.5", {"start": v(10198.1, 12.7) * mm, "end": v(10325.1, 12.7) * mm});
            skLineSegment(sketch, "E12.73.0.6", {"start": v(10325.1, 1041.4) * mm, "end": v(10198.1, 1041.4) * mm});
            skLineSegment(sketch, "E12.73.0.7", {"start": v(10325.1, 1066.8) * mm, "end": v(10198.1, 1066.8) * mm});
            skLineSegment(sketch, "E12.73.1.0", {"start": v(10198.1, 1041.4) * mm, "end": v(10198.1, 0) * mm});
            skLineSegment(sketch, "E12.73.1.1", {"start": v(10198.1, 1066.8) * mm, "end": v(10198.1, 2095.5) * mm});
            skLineSegment(sketch, "E12.73.1.2", {"start": v(10325.1, 12.7) * mm, "end": v(10325.1, 1041.4) * mm});
            skLineSegment(sketch, "E12.73.1.3", {"start": v(10325.1, 2095.5) * mm, "end": v(10325.1, 1066.8) * mm});
            skLineSegment(sketch, "E12.73.1.4", {"start": v(10198.1, 2095.5) * mm, "end": v(10325.1, 2095.5) * mm});
            skLineSegment(sketch, "E12.73.1.5", {"start": v(10198.1, 12.7) * mm, "end": v(10325.1, 12.7) * mm});
            skLineSegment(sketch, "E12.73.1.6", {"start": v(10325.1, 1041.4) * mm, "end": v(10198.1, 1041.4) * mm});
            skLineSegment(sketch, "E12.73.1.7", {"start": v(10325.1, 1066.8) * mm, "end": v(10198.1, 1066.8) * mm});
            skLineSegment(sketch, "E12.direction1", {"start": v(0, 0) * mm, "end": v(139.7, 0) * mm, "construction": true});
            skLineSegment(sketch, "E12.direction2", {"start": v(0, 0) * mm, "end": v(0, 0) * mm});
            skSolve(sketch);
        }
        {
            var Q0;
            Q0 = qSketchRegion(id + "F2", true);
            extrude(context, id + "F3", {"entities" : qUnion([Q0]), "operationType" : NewBodyOperationType.REMOVE, "oppositeDirection" : true, "depth" : 76.2 * mm, "offsetDistance" : 25.4 * mm});
        }
    });
